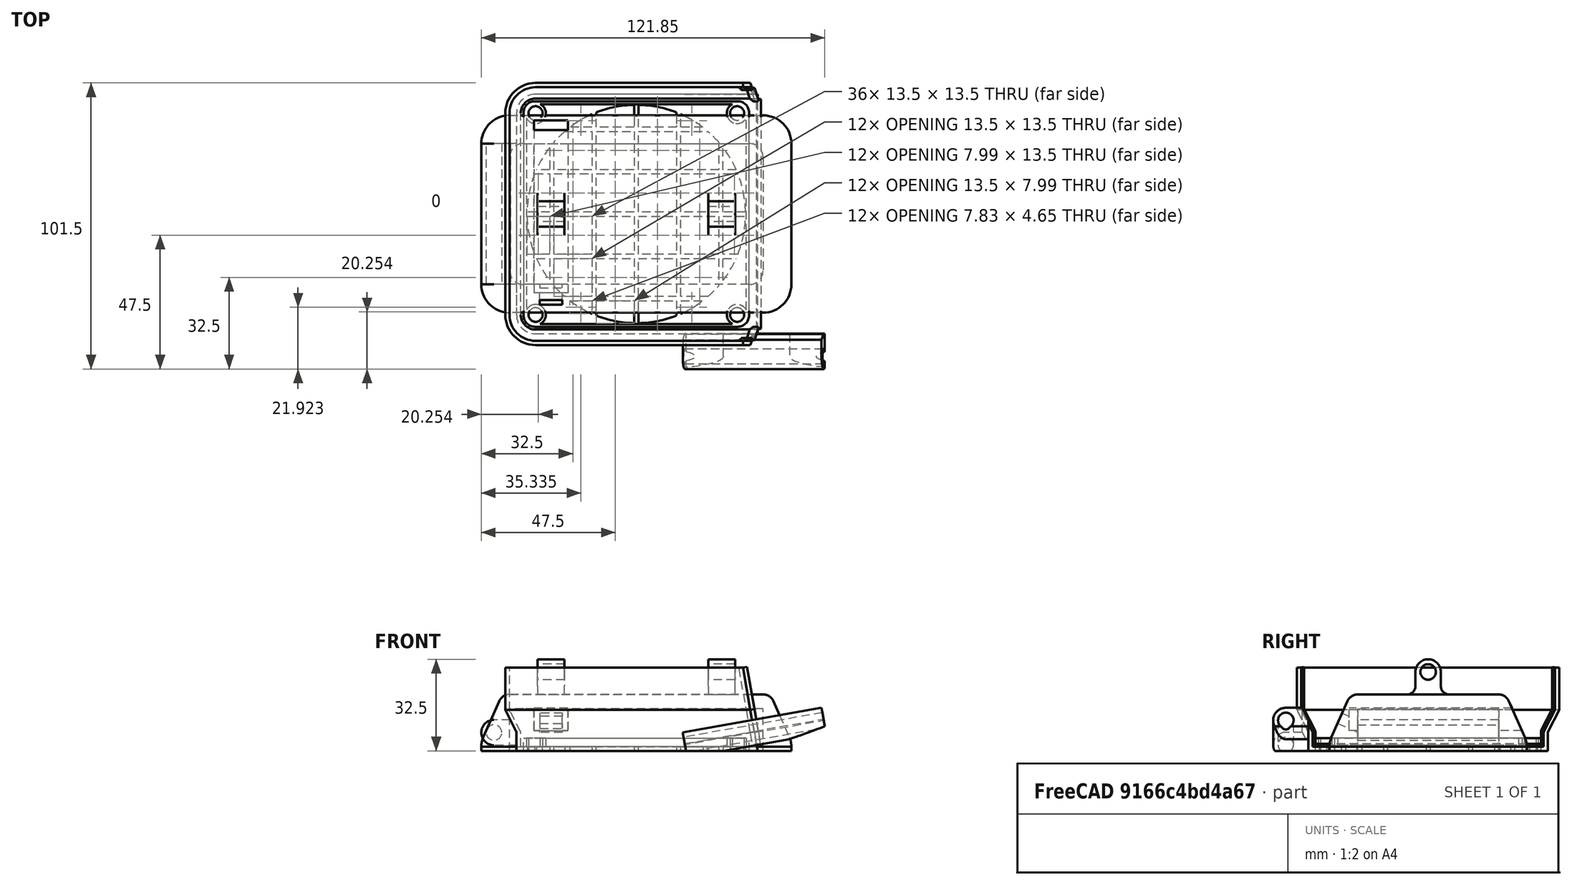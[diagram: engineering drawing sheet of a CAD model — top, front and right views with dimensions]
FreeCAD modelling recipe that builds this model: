
FCSTD DOCUMENT  (FreeCAD 1.0R39285 (Git))
Label: Solder Fume Extractor 2x80mm fans - v2
License: All rights reserved
LicenseURL: https://en.wikipedia.org/wiki/All_rights_reserved
objects: Sketcher::SketchObject×30, PartDesign::Pad×18, PartDesign::CoordinateSystem×13, App::Link×10, PartDesign::Pocket×8, PartDesign::LinearPattern×6, PartDesign::Body×5, PartDesign::AdditivePipe×3, App::DocumentObjectGroup×3, App::FeaturePython×1, Mesh::Feature×1, PartDesign::SubtractivePipe×1, App::Part×1
note: 180 computed .brp shape members not serialized (recipe doc carries the construction recipe); baked Part::Feature solids carry a one-line shape summary decoded from their .brp
EXTERNAL_REF file=Axial Fan.FCStd obj=FanHouse_TopMountHole
EXTERNAL_REF file=Axial Fan.FCStd obj=Assembly

FEATURE [Sketcher::SketchObject] Sketch
  ArcFitTolerance = 1e-06
  AttachmentSupport = -> [XY_Plane]
  FullyConstrained = true
  MakeInternals = false
  MapMode = 5
  sketch-geometry (13):
    g0: LineSegment StartX=-42.5 StartY=35.75 StartZ=0 EndX=-42.5 EndY=-35.75 EndZ=0
    g1: LineSegment StartX=-35.75 StartY=-42.5 StartZ=0 EndX=60 EndY=-42.5 EndZ=0
    g2: LineSegment StartX=60 StartY=-42.5 StartZ=0 EndX=60 EndY=42.5 EndZ=0
    g3: LineSegment StartX=60 StartY=42.5 StartZ=0 EndX=-35.75 EndY=42.5 EndZ=0
    g4: Circle CenterX=-35.75 CenterY=35.75 CenterZ=0 NormalX=0 NormalY=0 NormalZ=1 AngleXU=0 Radius=2.5
    g5: Circle CenterX=35.75 CenterY=35.75 CenterZ=0 NormalX=0 NormalY=0 NormalZ=1 AngleXU=0 Radius=2.5
    g6: Circle CenterX=-35.75 CenterY=-35.75 CenterZ=0 NormalX=0 NormalY=0 NormalZ=1 AngleXU=0 Radius=2.5
    g7: Circle CenterX=35.75 CenterY=-35.75 CenterZ=0 NormalX=0 NormalY=0 NormalZ=1 AngleXU=0 Radius=2.5
    g8: Circle CenterX=0 CenterY=0 CenterZ=0 NormalX=0 NormalY=0 NormalZ=1 AngleXU=0 Radius=38.75
    g9: ArcOfCircle CenterX=-35.75 CenterY=35.75 CenterZ=0 NormalX=0 NormalY=0 NormalZ=1 AngleXU=0 Radius=6.75 StartAngle=1.5708 EndAngle=3.14159
    g10: GeomPoint [constr] X=-42.5 Y=42.5 Z=0
    g11: ArcOfCircle CenterX=-35.75 CenterY=-35.75 CenterZ=0 NormalX=0 NormalY=0 NormalZ=1 AngleXU=0 Radius=6.75 StartAngle=3.14159 EndAngle=4.71239
    g12: GeomPoint [constr] X=-42.5 Y=-42.5 Z=0
  constraints (30):
    c: Coincident(g1,g2)
    c: Coincident(g2,g3)
    c: Vertical(g2)
    c: Horizontal(g1)
    c: Horizontal(g3)
    c: DistanceY(g12,g10) = 85
    c: Equal(g7,g5)
    c: Equal(g5,g4)
    c: Equal(g4,g6)
    c: Diameter(g7) = 5
    c: Symmetric(g7,g5,g-1)
    c: Symmetric(g5,g4,g-2)
    c: Vertical(g6,g4)
    c: Horizontal(g6,g7)
    c: DistanceX(g4,g5) = 71.5
    c: DistanceY(g6,g4) = 71.5
    c: Symmetric(g12,g10,g-1)
    c: Coincident(g8,g-1)
    c: Diameter(g8) = 77.5
    c: DistanceX(g10,g-1) = 42.5
    c: DistanceX(g1) = 60
    c: PointOnObject(g10,g0)
    c: PointOnObject(g10,g3)
    c: Tangent(g0,g9) = -1.5708
    c: Tangent(g3,g9) = -1.5708
    c: PointOnObject(g12,g1)
    c: Tangent(g0,g11) = -1.5708
    c: Tangent(g1,g11) = -1.5708
    c: Equal(g11,g9)
    c: Coincident(g9,g4)
FEATURE [PartDesign::Pad] Pad
  Direction = (0,0,1)
  Length = 1.5
  Length2 = 10
  Profile = -> Sketch
  ReferenceAxis = -> Sketch [N_Axis]
  Refine = true
  Suppressed = false
  Type = 0
FEATURE [Sketcher::SketchObject] Sketch001
  ArcFitTolerance = 1e-06
  AttachmentSupport = -> [Pad]
  ExternalGeometry = -> [Pad]
  FullyConstrained = true
  MakeInternals = false
  MapMode = 5
  Placement = pos=(0,0,1.5) rot=(0,0,1;0rad)
  sketch-geometry (12):
    g0: LineSegment StartX=60 StartY=42.5 StartZ=0 EndX=-35.75 EndY=42.5 EndZ=0
    g1: LineSegment StartX=-42.5 StartY=35.75 StartZ=0 EndX=-42.5 EndY=-35.75 EndZ=0
    g2: LineSegment StartX=-35.75 StartY=-42.5 StartZ=0 EndX=60 EndY=-42.5 EndZ=0
    g3: ArcOfCircle CenterX=-35.75 CenterY=-35.75 CenterZ=0 NormalX=0 NormalY=0 NormalZ=1 AngleXU=0 Radius=6.75 StartAngle=3.14159 EndAngle=4.71239
    g4: ArcOfCircle CenterX=-35.75 CenterY=35.75 CenterZ=0 NormalX=0 NormalY=0 NormalZ=1 AngleXU=0 Radius=6.75 StartAngle=1.5708 EndAngle=3.14159
    g5: LineSegment StartX=60 StartY=-42.5 StartZ=0 EndX=60 EndY=-41 EndZ=0
    g6: LineSegment StartX=60 StartY=-41 StartZ=0 EndX=-35.75 EndY=-41 EndZ=0
    g7: LineSegment StartX=-41 StartY=-35.75 StartZ=0 EndX=-41 EndY=35.75 EndZ=0
    g8: LineSegment StartX=-35.75 StartY=41 StartZ=0 EndX=60 EndY=41 EndZ=0
    g9: LineSegment StartX=60 StartY=41 StartZ=0 EndX=60 EndY=42.5 EndZ=0
    g10: ArcOfCircle CenterX=-35.75 CenterY=-35.75 CenterZ=0 NormalX=0 NormalY=0 NormalZ=1 AngleXU=0 Radius=5.25 StartAngle=3.14159 EndAngle=4.71239
    g11: ArcOfCircle CenterX=-35.75 CenterY=35.75 CenterZ=0 NormalX=0 NormalY=0 NormalZ=1 AngleXU=0 Radius=5.25 StartAngle=1.5708 EndAngle=3.14159
  constraints (30):
    c: Coincident(g0,g-3)
    c: Coincident(g0,g-4)
    c: Horizontal(g2)
    c: Symmetric(g2,g0,g-1)
    c: Equal(g2,g0)
    c: Coincident(g-5,g1)
    c: Coincident(g1,g-5)
    c: Coincident(g3,g2)
    c: Coincident(g3,g1)
    c: Coincident(g4,g1)
    c: Coincident(g4,g0)
    c: Equal(g4,g-4)
    c: Equal(g-4,g3)
    c: Coincident(g5,g2)
    c: Vertical(g5)
    c: Coincident(g6,g5)
    c: Horizontal(g6)
    c: Vertical(g7)
    c: Coincident(g9,g8)
    c: Coincident(g9,g0)
    c: Horizontal(g8)
    c: Vertical(g9)
    c: Equal(g5,g9)
    c: Equal(g6,g8)
    c: Tangent(g10,g6) = 1.5708
    c: Tangent(g10,g7) = 1.5708
    c: Tangent(g11,g7) = 1.5708
    c: Tangent(g11,g8) = 1.5708
    c: DistanceY(g5,g5) = 1.5
    c: Coincident(g11,g4)
FEATURE [PartDesign::Pad] Pad001
  BaseFeature = -> Pad
  Direction = (0,0,1)
  Length = 5
  Length2 = 10
  Profile = -> Sketch001
  ReferenceAxis = -> Sketch001 [N_Axis]
  Refine = true
  Suppressed = false
  Type = 0
FEATURE [Sketcher::SketchObject] Sketch002
  ArcFitTolerance = 1e-06
  AttachmentSupport = -> [Pad001]
  ExternalGeometry = -> [Pad001]
  FullyConstrained = true
  MakeInternals = false
  MapMode = 5
  Placement = pos=(60,0,0) rot=(0.57735,0.57735,0.57735;2.0944rad)
  sketch-geometry (9):
    g0: LineSegment StartX=41.1112 StartY=6.9583 StartZ=0 EndX=45 EndY=14.5 EndZ=0
    g1: LineSegment [constr] StartX=45 StartY=14.5 StartZ=0 EndX=46.5 EndY=14.5 EndZ=0
    g2: LineSegment StartX=46.5 StartY=14.5 StartZ=0 EndX=42.6112 EndY=6.9583 EndZ=0
    g3: ArcOfCircle CenterX=43.5 CenterY=6.5 CenterZ=0 NormalX=0 NormalY=0 NormalZ=1 AngleXU=0 Radius=1 StartAngle=2.66551 EndAngle=3.14159
    g4: ArcOfCircle CenterX=42 CenterY=6.5 CenterZ=0 NormalX=0 NormalY=0 NormalZ=1 AngleXU=0 Radius=1 StartAngle=2.66551 EndAngle=3.14159
    g5: LineSegment StartX=42.5 StartY=6.5 StartZ=0 EndX=41 EndY=6.5 EndZ=0
    g6: LineSegment StartX=45 StartY=14.5 StartZ=0 EndX=45 EndY=29.5 EndZ=0
    g7: LineSegment StartX=45 StartY=29.5 StartZ=0 EndX=46.5 EndY=29.5 EndZ=0
    g8: LineSegment StartX=46.5 StartY=29.5 StartZ=0 EndX=46.5 EndY=14.5 EndZ=0
  constraints (24):
    c: Coincident(g0,g1)
    c: Horizontal(g1)
    c: Coincident(g1,g2)
    c: Coincident(g3,g-3)
    c: Coincident(g4,g-3)
    c: Tangent(g4,g0) = 1.5708
    c: Tangent(g3,g2) = -1.5708
    c: Coincident(g5,g3)
    c: Coincident(g5,g4)
    c: Perpendicular(g3,g5)
    c: Perpendicular(g4,g5)
    c: Equal(g1,g5)
    c: Radius(g4) = 1
    c: DistanceY(g3,g1) = 8
    c: DistanceX(g3,g1) = 4
    c: Equal(g4,g3)
    c: Coincident(g0,g6)
    c: Vertical(g6)
    c: Coincident(g6,g7)
    c: Coincident(g7,g8)
    c: Coincident(g8,g1)
    c: Vertical(g8)
    c: Horizontal(g7)
    c: DistanceY(g8,g8) = 15
FEATURE [PartDesign::AdditivePipe] AdditivePipe
  AuxilleryCurvelinear = true
  AuxillerySpineTangent = false
  BaseFeature = -> Pad001
  Binormal = (0,0,0)
  Mode = 0
  Profile = -> Sketch002
  Refine = true
  Spine = -> Pad001 [Edge32,Edge33,Edge34,Edge35,Edge36]
  SpineTangent = false
  Suppressed = false
  Transformation = 0
  Transition = 0
FEATURE [Sketcher::SketchObject] Sketch003
  ArcFitTolerance = 1e-06
  AttachmentSupport = -> [XY_Plane]
  ExternalGeometry = -> [AdditivePipe]
  FullyConstrained = true
  MakeInternals = false
  MapMode = 5
  sketch-geometry (5):
    g0: LineSegment StartX=-30.75 StartY=42.5 StartZ=0 EndX=-30.75 EndY=-42.5 EndZ=0
    g1: LineSegment StartX=-30.75 StartY=-42.5 StartZ=0 EndX=-29.25 EndY=-42.5 EndZ=0
    g2: LineSegment StartX=-29.25 StartY=-42.5 StartZ=0 EndX=-29.25 EndY=42.5 EndZ=0
    g3: LineSegment StartX=-29.25 StartY=42.5 StartZ=0 EndX=-30.75 EndY=42.5 EndZ=0
    g4: GeomPoint [constr] X=-30 Y=0 Z=0
  constraints (13):
    c: Coincident(g0,g1)
    c: Coincident(g1,g2)
    c: Coincident(g2,g3)
    c: Coincident(g3,g0)
    c: Vertical(g0)
    c: Vertical(g2)
    c: Horizontal(g1)
    c: Horizontal(g3)
    c: Symmetric(g2,g0,g4)
    c: PointOnObject(g4,g-1)
    c: PointOnObject(g1,g-3)
    c: DistanceX(g3,g3) = 1.5
    c: DistanceX(g4,g-1) = 30
FEATURE [PartDesign::Pad] Pad002
  BaseFeature = -> AdditivePipe
  Direction = (0,0,1)
  Length = 10
  Length2 = 10
  Profile = -> Sketch003
  ReferenceAxis = -> Sketch003 [N_Axis]
  Refine = true
  Suppressed = false
  Type = 3
  UpToFace = -> AdditivePipe [Face4]
FEATURE [PartDesign::LinearPattern] LinearPattern
  BaseFeature = -> Pad002
  Direction = -> Sketch003 [H_Axis]
  Length = 60
  Mode = 0
  Occurrences = 5
  Offset = 15
  Originals = -> [Pad002]
  Refine = true
  Suppressed = false
  TransformMode = 0
FEATURE [Sketcher::SketchObject] Sketch004
  ArcFitTolerance = 1e-06
  AttachmentSupport = -> [XY_Plane]
  ExternalGeometry = -> [LinearPattern]
  FullyConstrained = true
  MakeInternals = false
  MapMode = 5
  sketch-geometry (5):
    g0: LineSegment StartX=42.5 StartY=29.25 StartZ=0 EndX=42.5 EndY=30.75 EndZ=0
    g1: LineSegment StartX=42.5 StartY=30.75 StartZ=0 EndX=-42.5 EndY=30.75 EndZ=0
    g2: LineSegment StartX=-42.5 StartY=30.75 StartZ=0 EndX=-42.5 EndY=29.25 EndZ=0
    g3: LineSegment StartX=-42.5 StartY=29.25 StartZ=0 EndX=42.5 EndY=29.25 EndZ=0
    g4: GeomPoint [constr] X=0 Y=30 Z=0
  constraints (13):
    c: Coincident(g0,g1)
    c: Coincident(g1,g2)
    c: Coincident(g2,g3)
    c: Coincident(g3,g0)
    c: Vertical(g0)
    c: Vertical(g2)
    c: Horizontal(g1)
    c: Horizontal(g3)
    c: Symmetric(g2,g0,g4)
    c: PointOnObject(g4,g-2)
    c: PointOnObject(g1,g-3)
    c: DistanceY(g4) = 30
    c: DistanceY(g0,g0) = 1.5
FEATURE [PartDesign::Pad] Pad003
  BaseFeature = -> LinearPattern
  Direction = (0,0,1)
  Length = 10
  Length2 = 10
  Profile = -> Sketch004
  ReferenceAxis = -> Sketch004 [N_Axis]
  Refine = true
  Suppressed = false
  Type = 3
  UpToFace = -> LinearPattern [Face68]
FEATURE [PartDesign::LinearPattern] LinearPattern001
  BaseFeature = -> Pad003
  Direction = -> Sketch004 [V_Axis]
  Length = 60
  Mode = 0
  Occurrences = 5
  Offset = 15
  Originals = -> [Pad003]
  Refine = true
  Reversed = true
  Suppressed = false
  TransformMode = 0
FEATURE [PartDesign::CoordinateSystem] FanMountHole
  AttacherType = Attacher::AttachEngine3D
  AttachmentSupport = -> [LinearPattern001]
  MapMode = 11
  Placement = pos=(-35.75,-35.75,0) rot=(0,0,1;1.5708rad)
FEATURE [PartDesign::CoordinateSystem] LCS_Origin
  AttacherType = Attacher::AttachEngine3D
  AttachmentSupport = -> [X_Axis001]
  MapMode = 2
FEATURE [App::DocumentObjectGroup] Constraints
FEATURE [App::FeaturePython] Variables  # WARN: FeaturePython — macro-defined, semantics opaque (R4)
  Type = App::PropertyContainer
FEATURE [App::DocumentObjectGroup] Configurations
FEATURE [Sketcher::SketchObject] Sketch005
  ArcFitTolerance = 1e-06
  AttachmentSupport = -> [XZ_Plane]
  ExternalGeometry = -> [LinearPattern001]
  FullyConstrained = true
  MakeInternals = false
  MapMode = 5
  Placement = pos=(0,0,0) rot=(1,0,0;1.5708rad)
  sketch-geometry (4):
    g0: LineSegment StartX=60 StartY=29.5 StartZ=0 EndX=60 EndY=0 EndZ=0
    g1: LineSegment StartX=60 StartY=0 StartZ=0 EndX=43 EndY=0 EndZ=0
    g2: LineSegment StartX=43 StartY=0 StartZ=0 EndX=37.7984 EndY=29.5 EndZ=0
    g3: LineSegment StartX=37.7984 StartY=29.5 StartZ=0 EndX=60 EndY=29.5 EndZ=0
  constraints (11):
    c: PointOnObject(g0,g-1)
    c: Vertical(g0)
    c: Coincident(g0,g1)
    c: PointOnObject(g1,g-1)
    c: Coincident(g1,g2)
    c: Coincident(g2,g3)
    c: Coincident(g3,g0)
    c: DistanceX(g-1,g1) = 43
    c: Angle(g1,g2) = 1.74533
    c: Coincident(g0,g-3)
    c: PointOnObject(g2,g-3)
FEATURE [PartDesign::Pocket] Pocket
  BaseFeature = -> LinearPattern001
  Direction = (0,1,-2e-16)
  Length = 5
  Length2 = 5
  Midplane = true
  Profile = -> Sketch005
  ReferenceAxis = -> Sketch005 [N_Axis]
  Refine = true
  Suppressed = false
  Type = 1
FEATURE [PartDesign::CoordinateSystem] OtherFanHolder
  AttacherType = Attacher::AttachEngine3D
  AttachmentSupport = -> [Pocket]
  MapMode = 45
  Placement = pos=(42.8701,0,0.736527) rot=(0.642788,0,0.766044;3.14159rad)
FEATURE [PartDesign::CoordinateSystem] FilterHolderMount
  AttacherType = Attacher::AttachEngine3D
  AttachmentSupport = -> [Pocket]
  MapMode = 11
  Placement = pos=(-35.75,35.75,1.5) rot=(0,0,1;1.5708rad)
FEATURE [Sketcher::SketchObject] Sketch006
  ArcFitTolerance = 1e-06
  AttachmentSupport = -> [XY_Plane002]
  FullyConstrained = true
  MakeInternals = false
  MapMode = 5
  sketch-geometry (15):
    g0: LineSegment StartX=40 StartY=-36 StartZ=0 EndX=40 EndY=36 EndZ=0
    g1: LineSegment StartX=36 StartY=40 StartZ=0 EndX=-36 EndY=40 EndZ=0
    g2: LineSegment StartX=-40 StartY=36 StartZ=0 EndX=-40 EndY=-36 EndZ=0
    g3: LineSegment StartX=-36 StartY=-40 StartZ=0 EndX=36 EndY=-40 EndZ=0
    g4: ArcOfCircle CenterX=36 CenterY=-36 CenterZ=0 NormalX=0 NormalY=0 NormalZ=1 AngleXU=0 Radius=4 StartAngle=4.71239 EndAngle=6.28319
    g5: ArcOfCircle CenterX=36 CenterY=36 CenterZ=0 NormalX=0 NormalY=0 NormalZ=1 AngleXU=0 Radius=4 StartAngle=2e-16 EndAngle=1.5708
    g6: ArcOfCircle CenterX=-36 CenterY=36 CenterZ=0 NormalX=0 NormalY=0 NormalZ=1 AngleXU=0 Radius=4 StartAngle=1.5708 EndAngle=3.14159
    g7: ArcOfCircle CenterX=-36 CenterY=-36 CenterZ=0 NormalX=0 NormalY=0 NormalZ=1 AngleXU=0 Radius=4 StartAngle=3.14159 EndAngle=4.71239
    g8: GeomPoint [constr] X=40 Y=-40 Z=0
    g9: GeomPoint [constr] X=-40 Y=40 Z=0
    g10: Circle CenterX=-35.75 CenterY=35.75 CenterZ=0 NormalX=0 NormalY=0 NormalZ=1 AngleXU=0 Radius=2.5
    g11: Circle CenterX=35.75 CenterY=35.75 CenterZ=0 NormalX=0 NormalY=0 NormalZ=1 AngleXU=0 Radius=2.5
    g12: Circle CenterX=35.75 CenterY=-35.75 CenterZ=0 NormalX=0 NormalY=0 NormalZ=1 AngleXU=0 Radius=2.5
    g13: Circle CenterX=-35.75 CenterY=-35.75 CenterZ=0 NormalX=0 NormalY=0 NormalZ=1 AngleXU=0 Radius=2.5
    g14: Circle CenterX=0 CenterY=0 CenterZ=0 NormalX=0 NormalY=0 NormalZ=1 AngleXU=0 Radius=38.75
  constraints (34):
    c: Tangent(g0,g4) = -1.5708
    c: Tangent(g0,g5) = -1.5708
    c: Tangent(g1,g5) = -1.5708
    c: Tangent(g1,g6) = -1.5708
    c: Tangent(g2,g6) = -1.5708
    c: Tangent(g2,g7) = -1.5708
    c: Tangent(g3,g7) = -1.5708
    c: Tangent(g3,g4) = -1.5708
    c: Vertical(g2)
    c: Horizontal(g1)
    c: Equal(g4,g5)
    c: Equal(g5,g6)
    c: Equal(g6,g7)
    c: PointOnObject(g8,g0)
    c: PointOnObject(g8,g3)
    c: PointOnObject(g9,g1)
    c: PointOnObject(g9,g2)
    c: Radius(g7) = 4
    c: Symmetric(g3,g3,g-2)
    c: Symmetric(g0,g0,g-1)
    c: Equal(g0,g3)
    c: DistanceY(g3,g1) = 80
    c: Equal(g10,g11)
    c: Equal(g11,g12)
    c: Equal(g12,g13)
    c: Symmetric(g10,g11,g-2)
    c: Symmetric(g11,g12,g-1)
    c: Horizontal(g12,g13)
    c: Vertical(g13,g10)
    c: DistanceY(g13,g10) = 71.5
    c: DistanceX(g10,g11) = 71.5
    c: Diameter(g11) = 5
    c: Coincident(g14,g-1)
    c: Diameter(g14) = 77.5
FEATURE [PartDesign::Pad] Pad004
  Direction = (0,0,1)
  Length = 1.5
  Length2 = 10
  Profile = -> Sketch006
  ReferenceAxis = -> Sketch006 [N_Axis]
  Refine = true
  Suppressed = false
  Type = 0
FEATURE [Sketcher::SketchObject] Sketch007
  ArcFitTolerance = 1e-06
  AttachmentSupport = -> [XY_Plane002]
  ExternalGeometry = -> [Pad004]
  FullyConstrained = true
  MakeInternals = false
  MapMode = 5
  sketch-geometry (5):
    g0: LineSegment StartX=-29.25 StartY=-40 StartZ=0 EndX=-29.25 EndY=40 EndZ=0
    g1: LineSegment StartX=-29.25 StartY=40 StartZ=0 EndX=-30.75 EndY=40 EndZ=0
    g2: LineSegment StartX=-30.75 StartY=40 StartZ=0 EndX=-30.75 EndY=-40 EndZ=0
    g3: LineSegment StartX=-30.75 StartY=-40 StartZ=0 EndX=-29.25 EndY=-40 EndZ=0
    g4: GeomPoint [constr] X=-30 Y=0 Z=0
  constraints (13):
    c: Coincident(g0,g1)
    c: Coincident(g1,g2)
    c: Coincident(g2,g3)
    c: Coincident(g3,g0)
    c: Vertical(g0)
    c: Vertical(g2)
    c: Horizontal(g1)
    c: Horizontal(g3)
    c: Symmetric(g2,g0,g4)
    c: PointOnObject(g4,g-1)
    c: PointOnObject(g1,g-3)
    c: DistanceX(g4,g-1) = 30
    c: DistanceX(g1,g1) = 1.5
FEATURE [PartDesign::Pad] Pad005
  BaseFeature = -> Pad004
  Direction = (0,0,1)
  Length = 10
  Length2 = 10
  Profile = -> Sketch007
  ReferenceAxis = -> Sketch007 [N_Axis]
  Refine = true
  Suppressed = false
  Type = 3
  UpToFace = -> Pad004 [Face15]
FEATURE [PartDesign::LinearPattern] LinearPattern002
  BaseFeature = -> Pad005
  Direction = -> Sketch007 [H_Axis]
  Length = 60
  Mode = 0
  Occurrences = 5
  Offset = 15
  Originals = -> [Pad005]
  Refine = true
  Suppressed = false
  TransformMode = 0
FEATURE [Sketcher::SketchObject] Sketch008
  ArcFitTolerance = 1e-06
  AttachmentSupport = -> [XY_Plane002]
  ExternalGeometry = -> [LinearPattern002]
  FullyConstrained = true
  MakeInternals = false
  MapMode = 5
  sketch-geometry (5):
    g0: LineSegment StartX=40 StartY=-30.75 StartZ=0 EndX=40 EndY=-29.25 EndZ=0
    g1: LineSegment StartX=40 StartY=-29.25 StartZ=0 EndX=-40 EndY=-29.25 EndZ=0
    g2: LineSegment StartX=-40 StartY=-29.25 StartZ=0 EndX=-40 EndY=-30.75 EndZ=0
    g3: LineSegment StartX=-40 StartY=-30.75 StartZ=0 EndX=40 EndY=-30.75 EndZ=0
    g4: GeomPoint [constr] X=0 Y=-30 Z=0
  constraints (13):
    c: Coincident(g0,g1)
    c: Coincident(g1,g2)
    c: Coincident(g2,g3)
    c: Coincident(g3,g0)
    c: Vertical(g0)
    c: Vertical(g2)
    c: Horizontal(g1)
    c: Horizontal(g3)
    c: Symmetric(g2,g0,g4)
    c: PointOnObject(g4,g-2)
    c: PointOnObject(g1,g-3)
    c: DistanceY(g4,g-1) = 30
    c: DistanceY(g0,g0) = 1.5
FEATURE [PartDesign::Pad] Pad006
  BaseFeature = -> LinearPattern002
  Direction = (0,0,1)
  Length = 10
  Length2 = 10
  Profile = -> Sketch008
  ReferenceAxis = -> Sketch008 [N_Axis]
  Refine = true
  Suppressed = false
  Type = 3
  UpToFace = -> LinearPattern002 [Face32]
FEATURE [PartDesign::LinearPattern] LinearPattern003
  BaseFeature = -> Pad006
  Direction = -> Sketch008 [V_Axis]
  Length = 60
  Mode = 0
  Occurrences = 5
  Offset = 15
  Originals = -> [Pad006]
  Refine = true
  Suppressed = false
  TransformMode = 0
FEATURE [Sketcher::SketchObject] Sketch009
  ArcFitTolerance = 1e-06
  AttachmentSupport = -> [LinearPattern003]
  ExternalGeometry = -> [LinearPattern003]
  FullyConstrained = true
  MakeInternals = false
  MapMode = 5
  Placement = pos=(0,0,1.5) rot=(0,0,1;0rad)
  sketch-geometry (20):
    g0: LineSegment StartX=-40 StartY=36 StartZ=0 EndX=-40 EndY=-36 EndZ=0
    g1: LineSegment StartX=-36 StartY=-40 StartZ=0 EndX=36 EndY=-40 EndZ=0
    g2: LineSegment StartX=40 StartY=-36 StartZ=0 EndX=40 EndY=36 EndZ=0
    g3: LineSegment StartX=36 StartY=40 StartZ=0 EndX=-36 EndY=40 EndZ=0
    g4: ArcOfCircle CenterX=-36 CenterY=36 CenterZ=0 NormalX=0 NormalY=0 NormalZ=1 AngleXU=0 Radius=4 StartAngle=1.5708 EndAngle=3.14159
    g5: ArcOfCircle CenterX=-36 CenterY=-36 CenterZ=0 NormalX=0 NormalY=0 NormalZ=1 AngleXU=0 Radius=4 StartAngle=3.14159 EndAngle=4.71239
    g6: ArcOfCircle CenterX=36 CenterY=-36 CenterZ=0 NormalX=0 NormalY=0 NormalZ=1 AngleXU=0 Radius=4 StartAngle=4.71239 EndAngle=6.28319
    g7: ArcOfCircle CenterX=36 CenterY=36 CenterZ=0 NormalX=0 NormalY=0 NormalZ=1 AngleXU=0 Radius=4 StartAngle=-9e-16 EndAngle=1.5708
    g8: GeomPoint [constr] X=-40 Y=40 Z=0
    g9: GeomPoint [constr] X=40 Y=-40 Z=0
    g10: LineSegment StartX=-39 StartY=36 StartZ=0 EndX=-39 EndY=-36 EndZ=0
    g11: LineSegment StartX=-36 StartY=-39 StartZ=0 EndX=36 EndY=-39 EndZ=0
    g12: LineSegment StartX=39 StartY=-36 StartZ=0 EndX=39 EndY=36 EndZ=0
    g13: LineSegment StartX=36 StartY=39 StartZ=0 EndX=-36 EndY=39 EndZ=0
    g14: ArcOfCircle CenterX=-36 CenterY=36 CenterZ=0 NormalX=0 NormalY=0 NormalZ=1 AngleXU=0 Radius=3 StartAngle=1.5708 EndAngle=3.14159
    g15: ArcOfCircle CenterX=-36 CenterY=-36 CenterZ=0 NormalX=0 NormalY=0 NormalZ=1 AngleXU=0 Radius=3 StartAngle=3.14159 EndAngle=4.71239
    g16: ArcOfCircle CenterX=36 CenterY=-36 CenterZ=0 NormalX=0 NormalY=0 NormalZ=1 AngleXU=0 Radius=3 StartAngle=4.71239 EndAngle=6.28319
    g17: ArcOfCircle CenterX=36 CenterY=36 CenterZ=0 NormalX=0 NormalY=0 NormalZ=1 AngleXU=0 Radius=3 StartAngle=-9e-16 EndAngle=1.5708
    g18: GeomPoint [constr] X=-39 Y=39 Z=0
    g19: GeomPoint [constr] X=39 Y=-39 Z=0
  constraints (44):
    c: Tangent(g0,g4) = -1.5708
    c: Tangent(g0,g5) = -1.5708
    c: Tangent(g1,g5) = -1.5708
    c: Tangent(g1,g6) = -1.5708
    c: Tangent(g2,g6) = -1.5708
    c: Tangent(g2,g7) = -1.5708
    c: Tangent(g3,g7) = -1.5708
    c: Tangent(g3,g4) = -1.5708
    c: Vertical(g0)
    c: Vertical(g2)
    c: Horizontal(g1)
    c: Equal(g4,g5)
    c: Equal(g5,g6)
    c: Equal(g6,g7)
    c: PointOnObject(g8,g0)
    c: PointOnObject(g8,g3)
    c: PointOnObject(g9,g1)
    c: PointOnObject(g9,g2)
    c: Coincident(g3,g-5)
    c: Equal(g-5,g7)
    c: Coincident(g3,g-3)
    c: Equal(g3,g2)
    c: Tangent(g10,g14) = -1.5708
    c: Tangent(g10,g15) = -1.5708
    c: Tangent(g11,g15) = -1.5708
    c: Tangent(g11,g16) = -1.5708
    c: Tangent(g12,g16) = -1.5708
    c: Tangent(g12,g17) = -1.5708
    c: Tangent(g13,g17) = -1.5708
    c: Tangent(g13,g14) = -1.5708
    c: Vertical(g10)
    c: Horizontal(g11)
    c: Equal(g14,g15)
    c: Equal(g15,g16)
    c: Equal(g16,g17)
    c: PointOnObject(g18,g10)
    c: PointOnObject(g18,g13)
    c: PointOnObject(g19,g11)
    c: PointOnObject(g19,g12)
    c: Symmetric(g12,g12,g-1)
    c: Symmetric(g13,g13,g-2)
    c: Equal(g11,g12)
    c: DistanceX(g12,g2) = 1
    c: Horizontal(g2,g12)
FEATURE [PartDesign::Pad] Pad007
  BaseFeature = -> LinearPattern003
  Direction = (0,0,1)
  Length = 3
  Length2 = 10
  Profile = -> Sketch009
  ReferenceAxis = -> Sketch009 [N_Axis]
  Refine = true
  Suppressed = false
  Type = 0
FEATURE [PartDesign::CoordinateSystem] FanHolder
  AttacherType = Attacher::AttachEngine3D
  AttachmentOffset = pos=(0,0,3) rot=(0,0,1;0rad)
  AttachmentSupport = -> [Pad007]
  MapMode = 11
  Placement = pos=(-35.75,35.75,4.5) rot=(0,0,1;1.5708rad)
FEATURE [Sketcher::SketchObject] Sketch010
  ArcFitTolerance = 1e-06
  AttachmentSupport = -> [XZ_Plane]
  ExternalGeometry = -> [Pocket]
  FullyConstrained = true
  MakeInternals = false
  MapMode = 5
  Placement = pos=(0,0,0) rot=(1,0,0;1.5708rad)
  sketch-geometry (7):
    g0: ArcOfCircle CenterX=-43.5 CenterY=6.5 CenterZ=0 NormalX=0 NormalY=0 NormalZ=1 AngleXU=0 Radius=1 StartAngle=-2.4e-14 EndAngle=0.476081
    g1: LineSegment StartX=-42.5 StartY=6.5 StartZ=0 EndX=-42.5 EndY=2 EndZ=0
    g2: LineSegment StartX=-42.5 StartY=2 StartZ=0 EndX=-50.5 EndY=2 EndZ=0
    g3: LineSegment StartX=-42.6112 StartY=6.9583 StartZ=0 EndX=-44.6953 EndY=11 EndZ=0
    g4: LineSegment StartX=-44.6953 StartY=11 StartZ=0 EndX=-50.5 EndY=11 EndZ=0
    g5: ArcOfCircle CenterX=-50.5 CenterY=6.5 CenterZ=0 NormalX=0 NormalY=0 NormalZ=1 AngleXU=0 Radius=4.5 StartAngle=1.5708 EndAngle=4.71239
    g6: Circle CenterX=-50.5 CenterY=6.5 CenterZ=0 NormalX=0 NormalY=0 NormalZ=1 AngleXU=0 Radius=2.75
  constraints (18):
    c: Coincident(g0,g-5)
    c: Coincident(g0,g-5)
    c: Equal(g-5,g0)
    c: Coincident(g1,g0)
    c: PointOnObject(g1,g-3)
    c: Coincident(g2,g1)
    c: Horizontal(g2)
    c: Coincident(g3,g0)
    c: PointOnObject(g3,g-4)
    c: Horizontal(g4)
    c: Tangent(g5,g4) = -1.5708
    c: Tangent(g5,g2) = 1.5708
    c: Diameter(g5) = 9
    c: Diameter(g6) = 5.5
    c: Coincident(g6,g5)
    c: Horizontal(g0,g5)
    c: Coincident(g3,g4)
    c: DistanceX(g5,g-4) = 4
FEATURE [PartDesign::Pad] Pad008
  BaseFeature = -> Pocket
  Direction = (0,-1,2e-16)
  Length = 50
  Length2 = 10
  Midplane = true
  Profile = -> Sketch010
  ReferenceAxis = -> Sketch010 [N_Axis]
  Refine = true
  Suppressed = false
  Type = 0
FEATURE [Sketcher::SketchObject] Sketch011
  ArcFitTolerance = 1e-06
  AttachmentSupport = -> [Pad008]
  ExternalGeometry = -> [Pad008]
  FullyConstrained = true
  MakeInternals = false
  MapMode = 5
  Placement = pos=(41.7034,1.6e-15,7.35343) rot=(0.540716,0.540716,0.6444;1.99673rad)
  sketch-geometry (7):
    g0: ArcOfCircle CenterX=-43.0908 CenterY=-0.761797 CenterZ=0 NormalX=0 NormalY=0 NormalZ=1 AngleXU=0 Radius=0.6 StartAngle=6.10761 EndAngle=6.92787
    g1: LineSegment StartX=-44.66 StartY=3.6334 StartZ=0 EndX=-42.6112 EndY=-0.401229 EndZ=0
    g2: LineSegment StartX=-42.5 StartY=-5.3666 StartZ=0 EndX=-42.5 EndY=-0.866599 EndZ=0
    g3: LineSegment StartX=-42.5 StartY=-5.3666 StartZ=0 EndX=-50.5 EndY=-5.3666 EndZ=0
    g4: LineSegment StartX=-44.66 StartY=3.6334 StartZ=0 EndX=-50.5 EndY=3.6334 EndZ=0
    g5: ArcOfCircle CenterX=-50.5 CenterY=-0.866599 CenterZ=0 NormalX=0 NormalY=0 NormalZ=1 AngleXU=0 Radius=4.5 StartAngle=1.5708 EndAngle=4.71239
    g6: Circle CenterX=-50.5 CenterY=-0.866599 CenterZ=0 NormalX=0 NormalY=0 NormalZ=1 AngleXU=0 Radius=2.75
  constraints (18):
    c: Coincident(g0,g-3)
    c: Coincident(g0,g-4)
    c: Radius(g0) = 0.6
    c: Coincident(g3,g2)
    c: Horizontal(g3)
    c: Coincident(g4,g1)
    c: Horizontal(g4)
    c: Tangent(g5,g4) = -1.5708
    c: Tangent(g5,g3) = 1.5708
    c: Diameter(g5) = 9
    c: Horizontal(g5,g2)
    c: Coincident(g6,g5)
    c: Diameter(g6) = 5.5
    c: DistanceX(g5,g-4) = 4
    c: Coincident(g2,g0)
    c: PointOnObject(g1,g-4)
    c: PointOnObject(g2,g-3)
    c: Coincident(g0,g1)
FEATURE [PartDesign::Pad] Pad009
  BaseFeature = -> Pad008
  Direction = (0.984808,-1e-16,0.173648)
  Length = 50
  Length2 = 10
  Midplane = true
  Profile = -> Sketch011
  ReferenceAxis = -> Sketch011 [N_Axis]
  Refine = true
  Suppressed = false
  Type = 0
FEATURE [Mesh::Feature] base_mount
FEATURE [Sketcher::SketchObject] Sketch014
  ArcFitTolerance = 1e-06
  AttachmentSupport = -> [XY_Plane004]
  FullyConstrained = true
  MakeInternals = false
  MapMode = 5
  sketch-geometry (13):
    g0: LineSegment StartX=-42.5 StartY=35.75 StartZ=0 EndX=-42.5 EndY=-35.75 EndZ=0
    g1: LineSegment StartX=-35.75 StartY=-42.5 StartZ=0 EndX=60 EndY=-42.5 EndZ=0
    g2: LineSegment StartX=60 StartY=-42.5 StartZ=0 EndX=60 EndY=42.5 EndZ=0
    g3: LineSegment StartX=60 StartY=42.5 StartZ=0 EndX=-35.75 EndY=42.5 EndZ=0
    g4: Circle CenterX=-35.75 CenterY=35.75 CenterZ=0 NormalX=0 NormalY=0 NormalZ=1 AngleXU=0 Radius=2.5
    g5: Circle CenterX=35.75 CenterY=35.75 CenterZ=0 NormalX=0 NormalY=0 NormalZ=1 AngleXU=0 Radius=2.5
    g6: Circle CenterX=-35.75 CenterY=-35.75 CenterZ=0 NormalX=0 NormalY=0 NormalZ=1 AngleXU=0 Radius=2.5
    g7: Circle CenterX=35.75 CenterY=-35.75 CenterZ=0 NormalX=0 NormalY=0 NormalZ=1 AngleXU=0 Radius=2.5
    g8: Circle CenterX=0 CenterY=0 CenterZ=0 NormalX=0 NormalY=0 NormalZ=1 AngleXU=0 Radius=38.75
    g9: ArcOfCircle CenterX=-35.75 CenterY=35.75 CenterZ=0 NormalX=0 NormalY=0 NormalZ=1 AngleXU=0 Radius=6.75 StartAngle=1.5708 EndAngle=3.14159
    g10: GeomPoint [constr] X=-42.5 Y=42.5 Z=0
    g11: ArcOfCircle CenterX=-35.75 CenterY=-35.75 CenterZ=0 NormalX=0 NormalY=0 NormalZ=1 AngleXU=0 Radius=6.75 StartAngle=3.14159 EndAngle=4.71239
    g12: GeomPoint [constr] X=-42.5 Y=-42.5 Z=0
  constraints (30):
    c: Coincident(g1,g2)
    c: Coincident(g2,g3)
    c: Vertical(g2)
    c: Horizontal(g1)
    c: Horizontal(g3)
    c: DistanceY(g12,g10) = 85
    c: Equal(g7,g5)
    c: Equal(g5,g4)
    c: Equal(g4,g6)
    c: Diameter(g7) = 5
    c: Symmetric(g7,g5,g-1)
    c: Symmetric(g5,g4,g-2)
    c: Vertical(g6,g4)
    c: Horizontal(g6,g7)
    c: DistanceX(g4,g5) = 71.5
    c: DistanceY(g6,g4) = 71.5
    c: Symmetric(g12,g10,g-1)
    c: Coincident(g8,g-1)
    c: Diameter(g8) = 77.5
    c: DistanceX(g10,g-1) = 42.5
    c: DistanceX(g1) = 60
    c: PointOnObject(g10,g0)
    c: PointOnObject(g10,g3)
    c: Tangent(g0,g9) = -1.5708
    c: Tangent(g3,g9) = -1.5708
    c: PointOnObject(g12,g1)
    c: Tangent(g0,g11) = -1.5708
    c: Tangent(g1,g11) = -1.5708
    c: Equal(g11,g9)
    c: Coincident(g9,g4)
FEATURE [PartDesign::Pad] Pad010
  Direction = (0,0,1)
  Length = 1.5
  Length2 = 10
  Profile = -> Sketch014
  ReferenceAxis = -> Sketch014 [N_Axis]
  Refine = true
  Suppressed = false
  Type = 0
FEATURE [Sketcher::SketchObject] Sketch015
  ArcFitTolerance = 1e-06
  AttachmentSupport = -> [Pad010]
  ExternalGeometry = -> [Pad010]
  FullyConstrained = true
  MakeInternals = false
  MapMode = 5
  Placement = pos=(0,0,1.5) rot=(0,0,1;0rad)
  sketch-geometry (12):
    g0: LineSegment StartX=60 StartY=42.5 StartZ=0 EndX=-35.75 EndY=42.5 EndZ=0
    g1: LineSegment StartX=-42.5 StartY=35.75 StartZ=0 EndX=-42.5 EndY=-35.75 EndZ=0
    g2: LineSegment StartX=-35.75 StartY=-42.5 StartZ=0 EndX=60 EndY=-42.5 EndZ=0
    g3: ArcOfCircle CenterX=-35.75 CenterY=-35.75 CenterZ=0 NormalX=0 NormalY=0 NormalZ=1 AngleXU=0 Radius=6.75 StartAngle=3.14159 EndAngle=4.71239
    g4: ArcOfCircle CenterX=-35.75 CenterY=35.75 CenterZ=0 NormalX=0 NormalY=0 NormalZ=1 AngleXU=0 Radius=6.75 StartAngle=1.5708 EndAngle=3.14159
    g5: LineSegment StartX=60 StartY=-42.5 StartZ=0 EndX=60 EndY=-41 EndZ=0
    g6: LineSegment StartX=60 StartY=-41 StartZ=0 EndX=-35.75 EndY=-41 EndZ=0
    g7: LineSegment StartX=-41 StartY=-35.75 StartZ=0 EndX=-41 EndY=35.75 EndZ=0
    g8: LineSegment StartX=-35.75 StartY=41 StartZ=0 EndX=60 EndY=41 EndZ=0
    g9: LineSegment StartX=60 StartY=41 StartZ=0 EndX=60 EndY=42.5 EndZ=0
    g10: ArcOfCircle CenterX=-35.75 CenterY=-35.75 CenterZ=0 NormalX=0 NormalY=0 NormalZ=1 AngleXU=0 Radius=5.25 StartAngle=3.14159 EndAngle=4.71239
    g11: ArcOfCircle CenterX=-35.75 CenterY=35.75 CenterZ=0 NormalX=0 NormalY=0 NormalZ=1 AngleXU=0 Radius=5.25 StartAngle=1.5708 EndAngle=3.14159
  constraints (30):
    c: Coincident(g0,g-3)
    c: Coincident(g0,g-4)
    c: Horizontal(g2)
    c: Symmetric(g2,g0,g-1)
    c: Equal(g2,g0)
    c: Coincident(g-5,g1)
    c: Coincident(g1,g-5)
    c: Coincident(g3,g2)
    c: Coincident(g3,g1)
    c: Coincident(g4,g1)
    c: Coincident(g4,g0)
    c: Equal(g4,g-4)
    c: Equal(g-4,g3)
    c: Coincident(g5,g2)
    c: Vertical(g5)
    c: Coincident(g6,g5)
    c: Horizontal(g6)
    c: Vertical(g7)
    c: Coincident(g9,g8)
    c: Coincident(g9,g0)
    c: Horizontal(g8)
    c: Vertical(g9)
    c: Equal(g5,g9)
    c: Equal(g6,g8)
    c: Tangent(g10,g6) = 1.5708
    c: Tangent(g10,g7) = 1.5708
    c: Tangent(g11,g7) = 1.5708
    c: Tangent(g11,g8) = 1.5708
    c: DistanceY(g5,g5) = 1.5
    c: Coincident(g11,g4)
FEATURE [PartDesign::Pad] Pad011
  BaseFeature = -> Pad010
  Direction = (0,0,1)
  Length = 5
  Length2 = 10
  Profile = -> Sketch015
  ReferenceAxis = -> Sketch015 [N_Axis]
  Refine = true
  Suppressed = false
  Type = 0
FEATURE [Sketcher::SketchObject] Sketch016
  ArcFitTolerance = 1e-06
  AttachmentSupport = -> [Pad011]
  ExternalGeometry = -> [Pad011]
  FullyConstrained = true
  MakeInternals = false
  MapMode = 5
  Placement = pos=(60,0,0) rot=(0.57735,0.57735,0.57735;2.0944rad)
  sketch-geometry (9):
    g0: LineSegment StartX=41.1112 StartY=6.9583 StartZ=0 EndX=45 EndY=14.5 EndZ=0
    g1: LineSegment [constr] StartX=45 StartY=14.5 StartZ=0 EndX=46.5 EndY=14.5 EndZ=0
    g2: LineSegment StartX=46.5 StartY=14.5 StartZ=0 EndX=42.6112 EndY=6.9583 EndZ=0
    g3: ArcOfCircle CenterX=43.5 CenterY=6.5 CenterZ=0 NormalX=0 NormalY=0 NormalZ=1 AngleXU=0 Radius=1 StartAngle=2.66551 EndAngle=3.14159
    g4: ArcOfCircle CenterX=42 CenterY=6.5 CenterZ=0 NormalX=0 NormalY=0 NormalZ=1 AngleXU=0 Radius=1 StartAngle=2.66551 EndAngle=3.14159
    g5: LineSegment StartX=42.5 StartY=6.5 StartZ=0 EndX=41 EndY=6.5 EndZ=0
    g6: LineSegment StartX=45 StartY=14.5 StartZ=0 EndX=45 EndY=29.5 EndZ=0
    g7: LineSegment StartX=45 StartY=29.5 StartZ=0 EndX=46.5 EndY=29.5 EndZ=0
    g8: LineSegment StartX=46.5 StartY=29.5 StartZ=0 EndX=46.5 EndY=14.5 EndZ=0
  constraints (24):
    c: Coincident(g0,g1)
    c: Horizontal(g1)
    c: Coincident(g1,g2)
    c: Coincident(g3,g-3)
    c: Coincident(g4,g-3)
    c: Tangent(g4,g0) = 1.5708
    c: Tangent(g3,g2) = -1.5708
    c: Coincident(g5,g3)
    c: Coincident(g5,g4)
    c: Perpendicular(g3,g5)
    c: Perpendicular(g4,g5)
    c: Equal(g1,g5)
    c: Radius(g4) = 1
    c: DistanceY(g3,g1) = 8
    c: DistanceX(g3,g1) = 4
    c: Equal(g4,g3)
    c: Coincident(g0,g6)
    c: Vertical(g6)
    c: Coincident(g6,g7)
    c: Horizontal(g7)
    c: Coincident(g7,g8)
    c: Coincident(g8,g1)
    c: Vertical(g8)
    c: DistanceY(g8,g8) = 15
FEATURE [PartDesign::AdditivePipe] AdditivePipe001
  AuxilleryCurvelinear = true
  AuxillerySpineTangent = false
  BaseFeature = -> Pad011
  Binormal = (0,0,0)
  Mode = 0
  Profile = -> Sketch016
  Refine = true
  Spine = -> Pad011 [Edge32,Edge33,Edge34,Edge35,Edge36]
  SpineTangent = false
  Suppressed = false
  Transformation = 0
  Transition = 0
FEATURE [Sketcher::SketchObject] Sketch017
  ArcFitTolerance = 1e-06
  AttachmentSupport = -> [XY_Plane004]
  ExternalGeometry = -> [AdditivePipe001]
  FullyConstrained = true
  MakeInternals = false
  MapMode = 5
  sketch-geometry (5):
    g0: LineSegment StartX=-30.75 StartY=42.5 StartZ=0 EndX=-30.75 EndY=-42.5 EndZ=0
    g1: LineSegment StartX=-30.75 StartY=-42.5 StartZ=0 EndX=-29.25 EndY=-42.5 EndZ=0
    g2: LineSegment StartX=-29.25 StartY=-42.5 StartZ=0 EndX=-29.25 EndY=42.5 EndZ=0
    g3: LineSegment StartX=-29.25 StartY=42.5 StartZ=0 EndX=-30.75 EndY=42.5 EndZ=0
    g4: GeomPoint [constr] X=-30 Y=0 Z=0
  constraints (13):
    c: Coincident(g0,g1)
    c: Coincident(g1,g2)
    c: Coincident(g2,g3)
    c: Coincident(g3,g0)
    c: Vertical(g0)
    c: Vertical(g2)
    c: Horizontal(g1)
    c: Horizontal(g3)
    c: Symmetric(g2,g0,g4)
    c: PointOnObject(g4,g-1)
    c: PointOnObject(g1,g-3)
    c: DistanceX(g3,g3) = 1.5
    c: DistanceX(g4,g-1) = 30
FEATURE [PartDesign::Pad] Pad012
  BaseFeature = -> AdditivePipe001
  Direction = (0,0,1)
  Length = 10
  Length2 = 10
  Profile = -> Sketch017
  ReferenceAxis = -> Sketch017 [N_Axis]
  Refine = true
  Suppressed = false
  Type = 3
  UpToFace = -> AdditivePipe001 [Face4]
FEATURE [PartDesign::LinearPattern] LinearPattern004
  BaseFeature = -> Pad012
  Direction = -> Sketch017 [H_Axis]
  Length = 60
  Mode = 0
  Occurrences = 5
  Offset = 15
  Originals = -> [Pad012]
  Refine = true
  Suppressed = false
  TransformMode = 0
FEATURE [Sketcher::SketchObject] Sketch018
  ArcFitTolerance = 1e-06
  AttachmentSupport = -> [XY_Plane004]
  ExternalGeometry = -> [LinearPattern004]
  FullyConstrained = true
  MakeInternals = false
  MapMode = 5
  sketch-geometry (5):
    g0: LineSegment StartX=42.5 StartY=29.25 StartZ=0 EndX=42.5 EndY=30.75 EndZ=0
    g1: LineSegment StartX=42.5 StartY=30.75 StartZ=0 EndX=-42.5 EndY=30.75 EndZ=0
    g2: LineSegment StartX=-42.5 StartY=30.75 StartZ=0 EndX=-42.5 EndY=29.25 EndZ=0
    g3: LineSegment StartX=-42.5 StartY=29.25 StartZ=0 EndX=42.5 EndY=29.25 EndZ=0
    g4: GeomPoint [constr] X=0 Y=30 Z=0
  constraints (13):
    c: Coincident(g0,g1)
    c: Coincident(g1,g2)
    c: Coincident(g2,g3)
    c: Coincident(g3,g0)
    c: Vertical(g0)
    c: Vertical(g2)
    c: Horizontal(g1)
    c: Horizontal(g3)
    c: Symmetric(g2,g0,g4)
    c: PointOnObject(g4,g-2)
    c: PointOnObject(g1,g-3)
    c: DistanceY(g4) = 30
    c: DistanceY(g0,g0) = 1.5
FEATURE [PartDesign::Pad] Pad013
  BaseFeature = -> LinearPattern004
  Direction = (0,0,1)
  Length = 10
  Length2 = 10
  Profile = -> Sketch018
  ReferenceAxis = -> Sketch018 [N_Axis]
  Refine = true
  Suppressed = false
  Type = 3
  UpToFace = -> LinearPattern004 [Face68]
FEATURE [PartDesign::LinearPattern] LinearPattern005
  BaseFeature = -> Pad013
  Direction = -> Sketch018 [V_Axis]
  Length = 60
  Mode = 0
  Occurrences = 5
  Offset = 15
  Originals = -> [Pad013]
  Refine = true
  Reversed = true
  Suppressed = false
  TransformMode = 0
FEATURE [PartDesign::CoordinateSystem] FanMountHole001
  AttacherType = Attacher::AttachEngine3D
  AttachmentSupport = -> [LinearPattern005]
  MapMode = 11
  Placement = pos=(-35.75,-35.75,0) rot=(0,0,1;1.5708rad)
FEATURE [Sketcher::SketchObject] Sketch019
  ArcFitTolerance = 1e-06
  AttachmentSupport = -> [XZ_Plane004]
  ExternalGeometry = -> [LinearPattern005]
  FullyConstrained = true
  MakeInternals = false
  MapMode = 5
  Placement = pos=(0,0,0) rot=(1,0,0;1.5708rad)
  sketch-geometry (4):
    g0: LineSegment StartX=60 StartY=29.5 StartZ=0 EndX=60 EndY=0 EndZ=0
    g1: LineSegment StartX=60 StartY=0 StartZ=0 EndX=43 EndY=0 EndZ=0
    g2: LineSegment StartX=43 StartY=0 StartZ=0 EndX=37.7984 EndY=29.5 EndZ=0
    g3: LineSegment StartX=37.7984 StartY=29.5 StartZ=0 EndX=60 EndY=29.5 EndZ=0
  constraints (11):
    c: PointOnObject(g0,g-1)
    c: Vertical(g0)
    c: Coincident(g0,g1)
    c: PointOnObject(g1,g-1)
    c: Coincident(g1,g2)
    c: Coincident(g2,g3)
    c: Coincident(g3,g0)
    c: DistanceX(g-1,g1) = 43
    c: Angle(g1,g2) = 1.74533
    c: Coincident(g0,g-3)
    c: PointOnObject(g2,g-3)
FEATURE [PartDesign::Pocket] Pocket002
  BaseFeature = -> LinearPattern005
  Direction = (0,1,-2e-16)
  Length = 5
  Length2 = 5
  Midplane = true
  Profile = -> Sketch019
  ReferenceAxis = -> Sketch019 [N_Axis]
  Refine = true
  Suppressed = false
  Type = 1
FEATURE [PartDesign::CoordinateSystem] FilterHolderMount001
  AttacherType = Attacher::AttachEngine3D
  AttachmentSupport = -> [Pocket002]
  MapMode = 11
  Placement = pos=(-35.75,35.75,1.5) rot=(0,0,1;1.5708rad)
FEATURE [PartDesign::CoordinateSystem] OtherFanHolder001
  AttacherType = Attacher::AttachEngine3D
  AttachmentSupport = -> [Pocket002]
  MapMode = 45
  Placement = pos=(42.8701,0,0.736527) rot=(0.642788,0,0.766044;3.14159rad)
FEATURE [Sketcher::SketchObject] Sketch022
  ArcFitTolerance = 1e-06
  FullyConstrained = true
  MakeInternals = false
  MapMode = 5
  Placement = pos=(41.7034,1.6e-15,7.35343) rot=(0.540716,0.540716,0.6444;1.99673rad)
  sketch-geometry (6):
    g0: ArcOfCircle CenterX=43.0908 CenterY=-0.761797 CenterZ=0 NormalX=0 NormalY=0 NormalZ=1 AngleXU=0 Radius=0.6 StartAngle=2.49691 EndAngle=3.31716
    g1: LineSegment StartX=44.66 StartY=3.6334 StartZ=0 EndX=42.6112 EndY=-0.401229 EndZ=0
    g2: LineSegment StartX=42.5 StartY=-5.3666 StartZ=0 EndX=42.5 EndY=-0.866599 EndZ=0
    g3: LineSegment StartX=42.5 StartY=-5.3666 StartZ=0 EndX=50.5 EndY=-5.3666 EndZ=0
    g4: LineSegment StartX=44.66 StartY=3.6334 StartZ=0 EndX=50.5 EndY=3.6334 EndZ=0
    g5: ArcOfCircle CenterX=50.5 CenterY=-0.866599 CenterZ=0 NormalX=0 NormalY=0 NormalZ=1 AngleXU=0 Radius=4.5 StartAngle=4.71239 EndAngle=7.85398
  constraints (16):
    c: Coincident(g0,g-3)
    c: Coincident(g0,g-4)
    c: Radius(g0) = 0.6
    c: Coincident(g3,g2)
    c: Horizontal(g3)
    c: Coincident(g4,g1)
    c: Horizontal(g4)
    c: Diameter(g5) = 9
    c: PointOnObject(g1,g-4)
    c: Horizontal(g5,g2)
    c: Tangent(g5,g3) = -1.5708
    c: Tangent(g5,g4) = 1.5708
    c: DistanceX(g-4,g5) = 4
    c: Coincident(g2,g0)
    c: Coincident(g0,g1)
    c: PointOnObject(g2,g-3)
FEATURE [PartDesign::Pocket] Pocket003
  BaseFeature = -> Pocket002
  Direction = (-0.984808,2e-16,-0.173648)
  Length = 50
  Length2 = 5
  Midplane = true
  Profile = -> Sketch022
  ReferenceAxis = -> Sketch022 [N_Axis]
  Refine = true
  Suppressed = false
  Type = 0
FEATURE [PartDesign::Body] Body003  label="Fan2Holder"
  AllowCompound = false
  Group = -> [Sketch014,Pad010,Sketch015,Pad011,Sketch016,AdditivePipe001,Sketch017,Pad012,LinearPattern004,Sketch018,Pad013,LinearPattern005,FanMountHole001,Sketch019,Pocket002,OtherFanHolder001,FilterHolderMount001,Sketch022,Pocket003]
  Origin = -> Origin004
  Tip = -> Pocket003
FEATURE [Sketcher::SketchObject] Sketch023
  ArcFitTolerance = 1e-06
  AttachmentSupport = -> [XY_Plane003]
  FullyConstrained = true
  MakeInternals = false
  MapMode = 5
  sketch-geometry (10):
    g0: LineSegment StartX=-55 StartY=25 StartZ=0 EndX=-55 EndY=-25 EndZ=0
    g1: LineSegment StartX=-45 StartY=-35 StartZ=0 EndX=45 EndY=-35 EndZ=0
    g2: LineSegment StartX=55 StartY=-25 StartZ=0 EndX=55 EndY=25 EndZ=0
    g3: LineSegment StartX=45 StartY=35 StartZ=0 EndX=-45 EndY=35 EndZ=0
    g4: ArcOfCircle CenterX=-45 CenterY=25 CenterZ=0 NormalX=0 NormalY=0 NormalZ=1 AngleXU=0 Radius=10 StartAngle=1.5708 EndAngle=3.14159
    g5: ArcOfCircle CenterX=-45 CenterY=-25 CenterZ=0 NormalX=0 NormalY=0 NormalZ=1 AngleXU=0 Radius=10 StartAngle=3.14159 EndAngle=4.71239
    g6: ArcOfCircle CenterX=45 CenterY=-25 CenterZ=0 NormalX=0 NormalY=0 NormalZ=1 AngleXU=0 Radius=10 StartAngle=4.71239 EndAngle=6.28319
    g7: ArcOfCircle CenterX=45 CenterY=25 CenterZ=0 NormalX=0 NormalY=0 NormalZ=1 AngleXU=0 Radius=10 StartAngle=1e-16 EndAngle=1.5708
    g8: GeomPoint [constr] X=-55 Y=35 Z=0
    g9: GeomPoint [constr] X=55 Y=-35 Z=0
  constraints (22):
    c: Tangent(g0,g4) = -1.5708
    c: Tangent(g0,g5) = -1.5708
    c: Tangent(g1,g5) = -1.5708
    c: Tangent(g1,g6) = -1.5708
    c: Tangent(g2,g6) = -1.5708
    c: Tangent(g2,g7) = -1.5708
    c: Tangent(g3,g7) = -1.5708
    c: Tangent(g3,g4) = -1.5708
    c: Vertical(g2)
    c: Horizontal(g1)
    c: Equal(g4,g5)
    c: Equal(g5,g6)
    c: Equal(g6,g7)
    c: PointOnObject(g8,g0)
    c: PointOnObject(g8,g3)
    c: PointOnObject(g9,g1)
    c: PointOnObject(g9,g2)
    c: Symmetric(g3,g3,g-2)
    c: Symmetric(g0,g0,g-1)
    c: DistanceX(g0,g2) = 110
    c: DistanceY(g1,g3) = 70
    c: Radius(g7) = 10
FEATURE [PartDesign::Pad] Pad014
  Direction = (0,0,1)
  Length = 20
  Length2 = 10
  Profile = -> Sketch023
  ReferenceAxis = -> Sketch023 [N_Axis]
  Refine = true
  Suppressed = false
  Type = 0
FEATURE [Sketcher::SketchObject] Sketch024
  ArcFitTolerance = 1e-06
  AttachmentSupport = -> [XZ_Plane003]
  ExternalGeometry = -> [Pad014]
  FullyConstrained = true
  MakeInternals = false
  MapMode = 5
  Placement = pos=(0,0,0) rot=(1,0,0;1.5708rad)
  sketch-geometry (5):
    g0: LineSegment StartX=55 StartY=20 StartZ=0 EndX=45 EndY=20 EndZ=0
    g1: ArcOfCircle CenterX=45 CenterY=16 CenterZ=0 NormalX=0 NormalY=0 NormalZ=1 AngleXU=0 Radius=4 StartAngle=0.413862 EndAngle=1.5708
    g2: ArcOfCircle CenterX=47 CenterY=1.5 CenterZ=0 NormalX=0 NormalY=0 NormalZ=1 AngleXU=0 Radius=8 StartAngle=3e-16 EndAngle=0.413862
    g3: LineSegment StartX=54.3246 StartY=4.71719 StartZ=0 EndX=48.6623 EndY=17.6086 EndZ=0
    g4: LineSegment StartX=55 StartY=20 StartZ=0 EndX=55 EndY=1.5 EndZ=0
  constraints (12):
    c: Horizontal(g0)
    c: Tangent(g1,g0) = -1.5708
    c: Tangent(g3,g2) = -1.5708
    c: Tangent(g3,g1) = -1.5708
    c: Coincident(g0,g-3)
    c: Coincident(g4,g0)
    c: PointOnObject(g4,g-3)
    c: Tangent(g4,g2) = 1.5708
    c: DistanceY(g2) = 1.5
    c: DistanceX(g0,g0) = 10
    c: Radius(g2) = 8
    c: Radius(g1) = 4
FEATURE [PartDesign::SubtractivePipe] SubtractivePipe
  AuxilleryCurvelinear = true
  AuxillerySpineTangent = false
  BaseFeature = -> Pad014
  Binormal = (0,0,0)
  Mode = 0
  Profile = -> Sketch024
  Refine = true
  Spine = -> Pad014 [Edge16,Edge19,Edge22,Edge24,Edge4,Edge7,Edge10,Edge13]
  SpineTangent = false
  Suppressed = false
  Transformation = 0
  Transition = 0
FEATURE [Sketcher::SketchObject] Sketch025
  ArcFitTolerance = 1e-06
  AttachmentSupport = -> [YZ_Plane003]
  ExternalGeometry = -> [SubtractivePipe]
  FullyConstrained = true
  MakeInternals = false
  MapMode = 5
  Placement = pos=(0,0,0) rot=(0.57735,0.57735,0.57735;2.0944rad)
  sketch-geometry (7):
    g0: LineSegment StartX=-7.5 StartY=20 StartZ=0 EndX=7.5 EndY=20 EndZ=0
    g1: ArcOfCircle CenterX=7.5 CenterY=23 CenterZ=0 NormalX=0 NormalY=0 NormalZ=1 AngleXU=0 Radius=3 StartAngle=3.14159 EndAngle=4.71239
    g2: ArcOfCircle CenterX=-7.5 CenterY=23 CenterZ=0 NormalX=0 NormalY=0 NormalZ=1 AngleXU=0 Radius=3 StartAngle=4.71239 EndAngle=6.28319
    g3: ArcOfCircle CenterX=8.84e-14 CenterY=28 CenterZ=0 NormalX=0 NormalY=0 NormalZ=1 AngleXU=0 Radius=4.5 StartAngle=-6.7475e-12 EndAngle=3.14159
    g4: LineSegment StartX=4.5 StartY=23 StartZ=0 EndX=4.5 EndY=28 EndZ=0
    g5: LineSegment StartX=-4.5 StartY=23 StartZ=0 EndX=-4.5 EndY=28 EndZ=0
    g6: Circle CenterX=8.84e-14 CenterY=28 CenterZ=0 NormalX=0 NormalY=0 NormalZ=1 AngleXU=0 Radius=2.75
  constraints (16):
    c: PointOnObject(g0,g-3)
    c: Symmetric(g0,g0,g-2)
    c: Vertical(g5)
    c: Tangent(g4,g3) = -1.5708
    c: Tangent(g4,g1) = 1.5708
    c: Tangent(g1,g0) = -1.5708
    c: Tangent(g2,g0) = -1.5708
    c: Tangent(g5,g2) = -1.5708
    c: Tangent(g5,g3) = 1.5708
    c: Vertical(g4)
    c: Equal(g1,g2)
    c: Diameter(g3) = 9
    c: Coincident(g6,g3)
    c: Diameter(g6) = 5.5
    c: Radius(g1) = 3
    c: DistanceY(g0,g3) = 8
FEATURE [PartDesign::Pad] Pad015
  BaseFeature = -> SubtractivePipe
  Direction = (1,0,0)
  Length = 70
  Length2 = 10
  Midplane = true
  Profile = -> Sketch025
  ReferenceAxis = -> Sketch025 [N_Axis]
  Refine = true
  Suppressed = false
  Type = 0
FEATURE [Sketcher::SketchObject] Sketch026
  ArcFitTolerance = 1e-06
  AttachmentSupport = -> [XZ_Plane003]
  ExternalGeometry = -> [Pad015]
  FullyConstrained = true
  MakeInternals = false
  MapMode = 5
  Placement = pos=(0,0,0) rot=(1,0,0;1.5708rad)
  sketch-geometry (5):
    g0: LineSegment StartX=-25.5 StartY=35 StartZ=0 EndX=-25.5 EndY=20 EndZ=0
    g1: LineSegment StartX=-25.5 StartY=20 StartZ=0 EndX=25.5 EndY=20 EndZ=0
    g2: LineSegment StartX=25.5 StartY=20 StartZ=0 EndX=25.5 EndY=35 EndZ=0
    g3: LineSegment StartX=25.5 StartY=35 StartZ=0 EndX=-25.5 EndY=35 EndZ=0
    g4: GeomPoint [constr] X=0 Y=27.5 Z=0
  constraints (13):
    c: Coincident(g0,g1)
    c: Coincident(g1,g2)
    c: Coincident(g2,g3)
    c: Coincident(g3,g0)
    c: Vertical(g0)
    c: Vertical(g2)
    c: Horizontal(g1)
    c: Horizontal(g3)
    c: Symmetric(g2,g0,g4)
    c: PointOnObject(g4,g-2)
    c: PointOnObject(g1,g-3)
    c: DistanceX(g3,g3) = 51
    c: DistanceY(g2,g2) = 15
FEATURE [PartDesign::Pocket] Pocket004
  BaseFeature = -> Pad015
  Direction = (0,1,-2e-16)
  Length = 5
  Length2 = 5
  Midplane = true
  Profile = -> Sketch026
  ReferenceAxis = -> Sketch026 [N_Axis]
  Refine = true
  Suppressed = false
  Type = 1
FEATURE [Sketcher::SketchObject] Sketch027
  ArcFitTolerance = 1e-06
  AttachmentSupport = -> [Pocket004]
  ExternalGeometry = -> [Pocket004]
  FullyConstrained = true
  MakeInternals = false
  MapMode = 5
  Placement = pos=(0,-30.5104,13.4011) rot=(1,0,0;1.15693rad)
  sketch-geometry (5):
    g0: LineSegment StartX=-34.25 StartY=0 StartZ=0 EndX=-34.25 EndY=-4 EndZ=0
    g1: LineSegment StartX=-34.25 StartY=-4 StartZ=0 EndX=-26.25 EndY=-4 EndZ=0
    g2: LineSegment StartX=-26.25 StartY=-4 StartZ=0 EndX=-26.25 EndY=0 EndZ=0
    g3: LineSegment StartX=-26.25 StartY=0 StartZ=0 EndX=-34.25 EndY=0 EndZ=0
    g4: LineSegment [constr] StartX=-30.25 StartY=0 StartZ=0 EndX=-30.25 EndY=15.2954 EndZ=0
  constraints (14):
    c: Coincident(g0,g1)
    c: Coincident(g1,g2)
    c: Coincident(g2,g3)
    c: Coincident(g3,g0)
    c: Vertical(g0)
    c: Vertical(g2)
    c: Horizontal(g1)
    c: Horizontal(g3)
    c: PointOnObject(g0,g-1)
    c: DistanceY(g2,g2) = 4
    c: DistanceX(g1,g1) = 8
    c: Symmetric(g3,g3,g4)
    c: Vertical(g4)
    c: Symmetric(g-3,g-3,g4)
FEATURE [PartDesign::Pocket] Pocket005
  BaseFeature = -> Pocket004
  Direction = (0,0.915575,-0.402148)
  Length = 10
  Length2 = 5
  Profile = -> Sketch027
  ReferenceAxis = -> Sketch027 [N_Axis]
  Refine = true
  Suppressed = false
  Type = 0
FEATURE [Sketcher::SketchObject] Sketch028
  ArcFitTolerance = 1e-06
  AttachmentSupport = -> [Pocket005]
  ExternalGeometry = -> [Pocket005]
  FullyConstrained = true
  MakeInternals = false
  MapMode = 5
  Placement = pos=(-2.8e-15,35,0) rot=(0,0.707107,0.707107;3.14159rad)
  sketch-geometry (6):
    g0: LineSegment StartX=24.25 StartY=15.1629 StartZ=0 EndX=24.25 EndY=7.16289 EndZ=0
    g1: LineSegment StartX=24.25 StartY=7.16289 StartZ=0 EndX=36.25 EndY=7.16289 EndZ=0
    g2: LineSegment StartX=36.25 StartY=7.16289 StartZ=0 EndX=36.25 EndY=15.1629 EndZ=0
    g3: LineSegment StartX=36.25 StartY=15.1629 StartZ=0 EndX=24.25 EndY=15.1629 EndZ=0
    g4: LineSegment [constr] StartX=30.25 StartY=15.1629 StartZ=0 EndX=30.25 EndY=23 EndZ=0
    g5: LineSegment [constr] StartX=45 StartY=11.1629 StartZ=0 EndX=36.25 EndY=11.1629 EndZ=0
  constraints (16):
    c: Coincident(g0,g1)
    c: Coincident(g1,g2)
    c: Coincident(g2,g3)
    c: Coincident(g3,g0)
    c: Vertical(g0)
    c: Vertical(g2)
    c: Horizontal(g1)
    c: Horizontal(g3)
    c: Symmetric(g3,g3,g4)
    c: Symmetric(g-3,g-3,g4)
    c: Vertical(g4)
    c: DistanceX(g3,g3) = 12
    c: DistanceY(g2,g2) = 8
    c: Symmetric(g-4,g-4,g5)
    c: Symmetric(g2,g2,g5)
    c: Horizontal(g5)
FEATURE [PartDesign::Pocket] Pocket006
  BaseFeature = -> Pocket005
  Direction = (0,-1,2e-16)
  Length = 63
  Length2 = 5
  Profile = -> Sketch028
  ReferenceAxis = -> Sketch028 [N_Axis]
  Refine = true
  Suppressed = false
  Type = 0
FEATURE [Sketcher::SketchObject] Sketch029
  ArcFitTolerance = 1e-06
  AttachmentSupport = -> [Pocket006]
  ExternalGeometry = -> [Pocket006]
  FullyConstrained = true
  MakeInternals = false
  MapMode = 5
  Placement = pos=(0,0,0) rot=(1,0,0;3.14159rad)
  sketch-geometry (10):
    g0: LineSegment StartX=-45 StartY=20 StartZ=0 EndX=-45 EndY=-20 EndZ=0
    g1: LineSegment StartX=-40 StartY=-25 StartZ=0 EndX=40 EndY=-25 EndZ=0
    g2: LineSegment StartX=45 StartY=-20 StartZ=0 EndX=45 EndY=20 EndZ=0
    g3: LineSegment StartX=40 StartY=25 StartZ=0 EndX=-40 EndY=25 EndZ=0
    g4: ArcOfCircle CenterX=-40 CenterY=20 CenterZ=0 NormalX=0 NormalY=0 NormalZ=1 AngleXU=0 Radius=5 StartAngle=1.5708 EndAngle=3.14159
    g5: ArcOfCircle CenterX=-40 CenterY=-20 CenterZ=0 NormalX=0 NormalY=0 NormalZ=1 AngleXU=0 Radius=5 StartAngle=3.14159 EndAngle=4.71239
    g6: ArcOfCircle CenterX=40 CenterY=-20 CenterZ=0 NormalX=0 NormalY=0 NormalZ=1 AngleXU=0 Radius=5 StartAngle=4.71239 EndAngle=6.28319
    g7: ArcOfCircle CenterX=40 CenterY=20 CenterZ=0 NormalX=0 NormalY=0 NormalZ=1 AngleXU=0 Radius=5 StartAngle=9.685e-13 EndAngle=1.5708
    g8: GeomPoint [constr] X=-45 Y=25 Z=0
    g9: GeomPoint [constr] X=45 Y=-25 Z=0
  constraints (22):
    c: Tangent(g0,g4) = -1.5708
    c: Tangent(g0,g5) = -1.5708
    c: Tangent(g1,g5) = -1.5708
    c: Tangent(g1,g6) = -1.5708
    c: Tangent(g2,g6) = -1.5708
    c: Tangent(g2,g7) = -1.5708
    c: Tangent(g3,g7) = -1.5708
    c: Tangent(g3,g4) = -1.5708
    c: Vertical(g2)
    c: Horizontal(g1)
    c: Equal(g4,g5)
    c: Equal(g5,g6)
    c: Equal(g6,g7)
    c: PointOnObject(g8,g0)
    c: PointOnObject(g8,g3)
    c: PointOnObject(g9,g1)
    c: PointOnObject(g9,g2)
    c: Radius(g5) = 5
    c: Symmetric(g3,g3,g-2)
    c: Symmetric(g0,g0,g-1)
    c: DistanceX(g2,g-3) = 10
    c: DistanceY(g3,g-4) = 10
FEATURE [PartDesign::Pocket] Pocket007
  BaseFeature = -> Pocket006
  Direction = (0,0,1)
  Length = 15
  Length2 = 5
  Profile = -> Sketch029
  ReferenceAxis = -> Sketch029 [N_Axis]
  Refine = true
  Suppressed = false
  Type = 0
FEATURE [PartDesign::CoordinateSystem] Fan  label="FanHolders"
  AttacherType = Attacher::AttachEngine3D
  AttachmentSupport = -> [Pocket007]
  MapMode = 45
  Placement = pos=(0,1.014e-13,28) rot=(0.57735,0.57735,0.57735;2.0944rad)
FEATURE [PartDesign::CoordinateSystem] Bottom
  AttacherType = Attacher::AttachEngine3D
  AttachmentSupport = -> [Pocket007]
  MapMode = 45
  Placement = pos=(-2.3879e-12,-1.227e-13,0) rot=(0,0,1;1.5708rad)
FEATURE [PartDesign::Body] Body002  label="Base"
  AllowCompound = false
  Group = -> [Sketch023,Pad014,Sketch024,SubtractivePipe,Sketch025,Pad015,Sketch026,Pocket004,Sketch027,Pocket005,Sketch028,Pocket006,Sketch029,Pocket007,Fan,Bottom]
  Origin = -> Origin003
  Tip = -> Pocket007
FEATURE [Sketcher::SketchObject] Sketch030
  ArcFitTolerance = 1e-06
  AttachmentSupport = -> [XY_Plane005]
  FullyConstrained = true
  MakeInternals = false
  MapMode = 5
  sketch-geometry (10):
    g0: LineSegment StartX=-55 StartY=25 StartZ=0 EndX=-55 EndY=-25 EndZ=0
    g1: LineSegment StartX=-45 StartY=-35 StartZ=0 EndX=45 EndY=-35 EndZ=0
    g2: LineSegment StartX=55 StartY=-25 StartZ=0 EndX=55 EndY=25 EndZ=0
    g3: LineSegment StartX=45 StartY=35 StartZ=0 EndX=-45 EndY=35 EndZ=0
    g4: ArcOfCircle CenterX=-45 CenterY=25 CenterZ=0 NormalX=0 NormalY=0 NormalZ=1 AngleXU=0 Radius=10 StartAngle=1.5708 EndAngle=3.14159
    g5: ArcOfCircle CenterX=-45 CenterY=-25 CenterZ=0 NormalX=0 NormalY=0 NormalZ=1 AngleXU=0 Radius=10 StartAngle=3.14159 EndAngle=4.71239
    g6: ArcOfCircle CenterX=45 CenterY=-25 CenterZ=0 NormalX=0 NormalY=0 NormalZ=1 AngleXU=0 Radius=10 StartAngle=4.71239 EndAngle=6.28319
    g7: ArcOfCircle CenterX=45 CenterY=25 CenterZ=0 NormalX=0 NormalY=0 NormalZ=1 AngleXU=0 Radius=10 StartAngle=0 EndAngle=1.5708
    g8: GeomPoint [constr] X=-55 Y=35 Z=0
    g9: GeomPoint [constr] X=55 Y=-35 Z=0
  constraints (22):
    c: Tangent(g0,g4) = -1.5708
    c: Tangent(g0,g5) = -1.5708
    c: Tangent(g1,g5) = -1.5708
    c: Tangent(g1,g6) = -1.5708
    c: Tangent(g2,g6) = -1.5708
    c: Tangent(g2,g7) = -1.5708
    c: Tangent(g3,g7) = -1.5708
    c: Tangent(g3,g4) = -1.5708
    c: Vertical(g2)
    c: Horizontal(g1)
    c: Equal(g4,g5)
    c: Equal(g5,g6)
    c: Equal(g6,g7)
    c: PointOnObject(g8,g0)
    c: PointOnObject(g8,g3)
    c: PointOnObject(g9,g1)
    c: PointOnObject(g9,g2)
    c: Radius(g5) = 10
    c: Symmetric(g3,g3,g-2)
    c: Symmetric(g0,g0,g-1)
    c: DistanceX(g0,g2) = 110
    c: DistanceY(g1,g3) = 70
FEATURE [App::Link] Base  label="Base001"
  AttachedBy = #Bottom
  AttachedTo = Parent Assembly#LCS_Origin
  AttachmentOffset = pos=(0,0,0) rot=(0,0,1;1.5708rad)
  LinkPlacement = pos=(2.3879e-12,1.227e-13,0) rot=(0,0,1;0rad)
  LinkedObject = -> Body002
  Placement = pos=(2.3879e-12,1.227e-13,0) rot=(0,0,1;0rad)
  SolverId = Asm4EE
  expr: Placement = LCS_Origin.Placement * AttachmentOffset * Bottom.Placement ^ -1
FEATURE [App::Link] Fan1Holder  label="Fan1Holder001"
  AttachedBy = #Mount1
  AttachedTo = Base#Fan
  AttachmentOffset = pos=(0,0,0) rot=(0.707107,-0.707107,0;3.14159rad)
  LinkPlacement = pos=(2.3343e-12,6.5,78.5) rot=(-0.57735,0.57735,-0.57735;4.18879rad)
  LinkedObject = -> Body
  Placement = pos=(2.3343e-12,6.5,78.5) rot=(-0.57735,0.57735,-0.57735;4.18879rad)
  SolverId = Asm4EE
  expr: Placement = Base.Placement * Fan.Placement * AttachmentOffset * Mount1.Placement ^ -1
FEATURE [App::Link] Fan2Holder  label="Fan2Holder001"
  AttachedBy = #OtherFanHolder001
  AttachedTo = Fan1Holder#OtherFanHolder
  AttachmentOffset = pos=(0,0,0) rot=(1,0,0;3.14159rad)
  LinkPlacement = pos=(2.4492e-12,-8.20687,161.907) rot=(0.633687,0.633687,-0.443713;2.30637rad)
  LinkedObject = -> Body003
  Placement = pos=(2.4492e-12,-8.20687,161.907) rot=(0.633687,0.633687,-0.443713;2.30637rad)
  SolverId = Asm4EE
  expr: Placement = Fan1Holder.Placement * OtherFanHolder.Placement * AttachmentOffset * OtherFanHolder001.Placement ^ -1
FEATURE [App::Link] FilterHolder  label="FilterHolder001"
  AttachedBy = #FanHolder
  AttachedTo = Fan1Holder#FilterHolderMount
  AttachmentOffset = pos=(0,0,0) rot=(-0.707107,-0.707107,0;3.14159rad)
  LinkPlacement = pos=(2.3874e-12,0.5,78.5) rot=(-1,0,0;1.5708rad)
  LinkedObject = -> Body001
  Placement = pos=(2.3874e-12,0.5,78.5) rot=(-1,0,0;1.5708rad)
  SolverId = Asm4EE
  expr: Placement = Fan1Holder.Placement * FilterHolderMount.Placement * AttachmentOffset * FanHolder.Placement ^ -1
FEATURE [App::Link] FilterHolder001  label="FilterHolder002"
  AttachedBy = #FanHolder
  AttachedTo = Fan2Holder#FilterHolderMount001
  AttachmentOffset = pos=(0,0,0) rot=(-0.707107,-0.707107,0;3.14159rad)
  LinkPlacement = pos=(2.4869e-12,-13.845,159.855) rot=(0,-0.573576,-0.819152;3.14159rad)
  LinkedObject = -> Body001
  Placement = pos=(2.4869e-12,-13.845,159.855) rot=(0,-0.573576,-0.819152;3.14159rad)
  SolverId = Asm4EE
  expr: Placement = Fan2Holder.Placement * FilterHolderMount001.Placement * AttachmentOffset * FanHolder.Placement ^ -1
FEATURE [App::Link] _0mmAxialFan  label="80mmAxialFan"
  AttachedBy = #FanHouse_TopMountHole
  AttachedTo = Fan1Holder#FanMountHole
  AttachmentOffset = pos=(0,0,0) rot=(0,0,1;1.5708rad)
  LinkPlacement = pos=(2.1458e-12,31.5,78.5) rot=(0,0.707107,-0.707107;3.14159rad)
  LinkedObject = -> <external Axial Fan.FCStd>#Assembly
  Placement = pos=(2.1458e-12,31.5,78.5) rot=(0,0.707107,-0.707107;3.14159rad)
  SolverId = Asm4EE
  expr: Placement = Fan1Holder.Placement * FanMountHole.Placement * AttachmentOffset * Axial_Fan#FanHouse_TopMountHole.Placement ^ -1
FEATURE [App::Link] _0mmAxialFan001  label="80mmAxialFan001"
  AttachedBy = #FanHouse_TopMountHole
  AttachedTo = Fan2Holder#FanMountHole001
  AttachmentOffset = pos=(0,0,0) rot=(0,0,1;1.5708rad)
  LinkPlacement = pos=(2.2737e-12,15.2854,170.457) rot=(1,0,0;1.91986rad)
  LinkedObject = -> <external Axial Fan.FCStd>#Assembly
  Placement = pos=(2.2737e-12,15.2854,170.457) rot=(1,0,0;1.91986rad)
  SolverId = Asm4EE
  expr: Placement = Fan2Holder.Placement * FanMountHole001.Placement * AttachmentOffset * Axial_Fan#FanHouse_TopMountHole.Placement ^ -1
FEATURE [App::Link] BottomCover  label="BottomCover001"
  AttachedBy = #Base001
  AttachedTo = Base#Bottom
  LinkPlacement = pos=(8.91e-14,6.93e-14,-1.5) rot=(0,0,1;0rad)
  LinkedObject = -> Body004
  Placement = pos=(8.91e-14,6.93e-14,-1.5) rot=(0,0,1;0rad)
  SolverId = Asm4EE
  expr: Placement = Base.Placement * Bottom.Placement * AttachmentOffset * Base001.Placement ^ -1
FEATURE [PartDesign::Pad] Pad016
  Direction = (0,0,1)
  Length = 1.5
  Length2 = 10
  Profile = -> Sketch030
  ReferenceAxis = -> Sketch030 [N_Axis]
  Refine = true
  Suppressed = false
  Type = 0
FEATURE [PartDesign::CoordinateSystem] Base001  label="Base002"
  AttacherType = Attacher::AttachEngine3D
  AttachmentSupport = -> [Pad016]
  MapMode = 45
  Placement = pos=(-8.91e-14,-6.93e-14,1.5) rot=(0,0,1;1.5708rad)
FEATURE [PartDesign::Body] Body004  label="BottomCover"
  AllowCompound = false
  Group = -> [Sketch030,Base001,Pad016]
  Origin = -> Origin005
  Tip = -> Pad016
FEATURE [App::Link] Base002  label="Base003"
  AttachedBy = #Fan
  AttachedTo = Fan1Holder#Mount2
  AttachmentOffset = pos=(0,0,0) rot=(0,0,1;4.71239rad)
  LinkPlacement = pos=(50.5,27.5746,125.216) rot=(0.60812,-0.60812,0.510274;2.19793rad)
  LinkedObject = -> Body002
  Placement = pos=(50.5,27.5746,125.216) rot=(0.60812,-0.60812,0.510274;2.19793rad)
  SolverId = Asm4EE
  expr: Placement = Fan1Holder.Placement * Mount2.Placement * AttachmentOffset * Fan.Placement ^ -1
FEATURE [App::Link] BottomCover001  label="BottomCover002"
  AttachedBy = #Base001
  AttachedTo = Base002#Bottom
  LinkPlacement = pos=(50.5,29.0518,125.476) rot=(0.60812,-0.60812,0.510274;2.19793rad)
  LinkedObject = -> Body004
  Placement = pos=(50.5,29.0518,125.476) rot=(0.60812,-0.60812,0.510274;2.19793rad)
  SolverId = Asm4EE
  expr: Placement = Base002.Placement * Bottom.Placement * AttachmentOffset * Base001.Placement ^ -1
FEATURE [App::Part] Assembly
  AssemblyType = Part::Link
  Group = -> [LCS_Origin,Constraints,Variables,Configurations,Base,Fan1Holder,Fan2Holder,FilterHolder,FilterHolder001,_0mmAxialFan,_0mmAxialFan001,BottomCover,Base002,BottomCover001]
  Origin = -> Origin001
  Type = Assembly
FEATURE [Sketcher::SketchObject] Sketch031
  ArcFitTolerance = 1e-06
  AttachmentSupport = -> [XZ_Plane]
  FullyConstrained = true
  MakeInternals = false
  MapMode = 5
  Placement = pos=(0,0,0) rot=(1,0,0;1.5708rad)
  sketch-geometry (8):
    g0: LineSegment StartX=0 StartY=0 StartZ=0 EndX=0 EndY=-5 EndZ=0
    g1: LineSegment StartX=0 StartY=-5 StartZ=0 EndX=43 EndY=-5 EndZ=0
    g2: LineSegment StartX=43 StartY=-5 StartZ=0 EndX=43 EndY=1.24e-14 EndZ=0
    g3: LineSegment StartX=43 StartY=1.24e-14 StartZ=0 EndX=0 EndY=0 EndZ=0
    g4: LineSegment StartX=43 StartY=1.24e-14 StartZ=0 EndX=44.7101 EndY=-4.69846 EndZ=0
    g5: LineSegment StartX=44.7101 StartY=-4.69846 StartZ=0 EndX=85.1169 EndY=10.0084 EndZ=0
    g6: LineSegment StartX=85.1169 StartY=10.0084 StartZ=0 EndX=83.4068 EndY=14.7069 EndZ=0
    g7: LineSegment StartX=83.4068 StartY=14.7069 StartZ=0 EndX=43 EndY=1.24e-14 EndZ=0
  constraints (22):
    c: Angle(g-3,g-1) = 1.39626
    c: Coincident(g0,g1)
    c: Coincident(g1,g2)
    c: Coincident(g2,g3)
    c: Coincident(g3,g0)
    c: Vertical(g0)
    c: Vertical(g2)
    c: Horizontal(g1)
    c: Coincident(g0,g-1)
    c: Coincident(g2,g-3)
    c: DistanceY(g2,g2) = 5
    c: Coincident(g2,g4)
    c: Coincident(g4,g5)
    c: Coincident(g5,g6)
    c: Coincident(g6,g7)
    c: Coincident(g7,g4)
    c: Perpendicular(g7,g4)
    c: Perpendicular(g6,g7)
    c: Equal(g4,g6)
    c: Equal(g6,g2)
    c: Equal(g7,g1)
    c: Angle(g7,g-3) = 1.39626
FEATURE [PartDesign::Pocket] Pocket008
  BaseFeature = -> Pad009
  Direction = (0,1,-2e-16)
  Length = 5
  Length2 = 5
  Profile = -> Sketch031
  ReferenceAxis = -> Sketch031 [N_Axis]
  Refine = true
  Reversed = true
  Suppressed = false
  Type = 1
FEATURE [PartDesign::CoordinateSystem] Mount1
  AttacherType = Attacher::AttachEngine3D
  AttachmentSupport = -> [Pocket008]
  MapMode = 45
  Placement = pos=(-50.5,-7e-16,6.5) rot=(0,0.707107,0.707107;3.14159rad)
FEATURE [PartDesign::CoordinateSystem] Mount2
  AttacherType = Attacher::AttachEngine3D
  AttachmentOffset = pos=(0,0,25) rot=(0,0,1;0rad)
  AttachmentSupport = -> [Pocket008]
  MapMode = 11
  Placement = pos=(41.8539,-50.5,6.5) rot=(0.642788,0,0.766044;3.14159rad)
FEATURE [Sketcher::SketchObject] Sketch032
  ArcFitTolerance = 1e-06
  AttachmentSupport = -> [XZ_Plane]
  ExternalGeometry = -> [Pocket008]
  FullyConstrained = true
  MakeInternals = false
  MapMode = 5
  Placement = pos=(0,0,0) rot=(1,0,0;1.5708rad)
  sketch-geometry (7):
    g0: LineSegment StartX=41.2355 StartY=1.5 StartZ=0 EndX=42.7355 EndY=1.5 EndZ=0
    g1: LineSegment StartX=42.7355 StartY=1.5 StartZ=0 EndX=44.145 EndY=2.01303 EndZ=0
    g2: ArcOfCircle CenterX=41.2355 CenterY=2.10733 CenterZ=0 NormalX=0 NormalY=0 NormalZ=1 AngleXU=0 Radius=0.607328 StartAngle=4.71239 EndAngle=6.06406
    g3: ArcOfCircle CenterX=43.9373 CenterY=2.58373 CenterZ=0 NormalX=0 NormalY=0 NormalZ=1 AngleXU=0 Radius=0.607328 StartAngle=3.70978 EndAngle=5.06145
    g4: LineSegment StartX=42.3157 StartY=2.4414 StartZ=0 EndX=42.8081 EndY=2.52822 EndZ=0
    g5: ArcOfCircle CenterX=42.4211 CenterY=1.84329 CenterZ=0 NormalX=0 NormalY=0 NormalZ=1 AngleXU=0 Radius=0.607328 StartAngle=1.74533 EndAngle=2.92247
    g6: ArcOfCircle CenterX=42.9135 CenterY=1.93012 CenterZ=0 NormalX=0 NormalY=0 NormalZ=1 AngleXU=0 Radius=0.607328 StartAngle=0.568188 EndAngle=1.74533
  constraints (17):
    c: Coincident(g0,g-4)
    c: Horizontal(g0)
    c: Coincident(g0,g1)
    c: DistanceX(g0,g0) = 1.5
    c: Angle(g1,g-4) = 1.39626
    c: Symmetric(g4,g4,g-4)
    c: Tangent(g5,g4) = 1.5708
    c: Tangent(g5,g2) = 1.5708
    c: Tangent(g6,g4) = 1.5708
    c: Tangent(g6,g3) = 1.5708
    c: Tangent(g3,g1) = -1.5708
    c: Tangent(g2,g0) = -1.5708
    c: Equal(g2,g5)
    c: Equal(g5,g6)
    c: Equal(g6,g3)
    c: Distance(g0,g4) = 1
    c: Distance(g4) = 0.5
FEATURE [PartDesign::AdditivePipe] AdditivePipe002
  AuxilleryCurvelinear = true
  AuxillerySpineTangent = false
  BaseFeature = -> Pocket008
  Binormal = (0,0,0)
  Mode = 0
  Profile = -> Sketch032
  Refine = true
  Spine = -> Pocket008 [Edge31,Edge30,Edge29,Edge28,Edge32,Edge33,Edge34,Edge35,Edge27]
  SpineTangent = false
  Suppressed = false
  Transformation = 0
  Transition = 1
FEATURE [PartDesign::Body] Body  label="Fan1Holder"
  AllowCompound = false
  Group = -> [Sketch,Pad,Sketch001,Pad001,Sketch002,AdditivePipe,Sketch003,Pad002,LinearPattern,Sketch004,Pad003,LinearPattern001,FanMountHole,Sketch005,Pocket,OtherFanHolder,FilterHolderMount,Sketch010,Pad008,Sketch011,Pad009,Mount1,Mount2,Sketch031,Pocket008,Sketch032,AdditivePipe002]
  Origin = -> Origin
  Tip = -> AdditivePipe002
FEATURE [Sketcher::SketchObject] Sketch033
  ArcFitTolerance = 1e-06
  AttachmentSupport = -> [Pad007]
  ExternalGeometry = -> [Pad007]
  FullyConstrained = true
  MakeInternals = false
  MapMode = 5
  Placement = pos=(0,0,1.5) rot=(0,0,1;0rad)
  sketch-geometry (8):
    g0: Circle CenterX=35.75 CenterY=35.75 CenterZ=0 NormalX=0 NormalY=0 NormalZ=1 AngleXU=0 Radius=2.5
    g1: Circle CenterX=35.75 CenterY=35.75 CenterZ=0 NormalX=0 NormalY=0 NormalZ=1 AngleXU=0 Radius=3.64645
    g2: Circle CenterX=-35.75 CenterY=35.75 CenterZ=0 NormalX=0 NormalY=0 NormalZ=1 AngleXU=0 Radius=2.5
    g3: Circle CenterX=-35.75 CenterY=35.75 CenterZ=0 NormalX=0 NormalY=0 NormalZ=1 AngleXU=0 Radius=3.64645
    g4: Circle CenterX=-35.75 CenterY=-35.75 CenterZ=0 NormalX=0 NormalY=0 NormalZ=1 AngleXU=0 Radius=2.5
    g5: Circle CenterX=-35.75 CenterY=-35.75 CenterZ=0 NormalX=0 NormalY=0 NormalZ=1 AngleXU=0 Radius=3.64645
    g6: Circle CenterX=35.75 CenterY=-35.75 CenterZ=0 NormalX=0 NormalY=0 NormalZ=1 AngleXU=0 Radius=2.5
    g7: Circle CenterX=35.75 CenterY=-35.75 CenterZ=0 NormalX=0 NormalY=0 NormalZ=1 AngleXU=0 Radius=3.64645
  constraints (16):
    c: Coincident(g0,g-3)
    c: Coincident(g1,g0)
    c: Coincident(g2,g-6)
    c: Coincident(g3,g2)
    c: Coincident(g4,g-5)
    c: Coincident(g5,g4)
    c: Coincident(g6,g-4)
    c: Coincident(g7,g6)
    c: Equal(g6,g4)
    c: Equal(g4,g2)
    c: Equal(g2,g0)
    c: Equal(g0,g-4)
    c: Equal(g7,g1)
    c: Equal(g1,g3)
    c: Equal(g3,g5)
    c: Tangent(g7,g-7)
FEATURE [PartDesign::Pad] Pad017
  BaseFeature = -> Pad007
  Direction = (0,0,1)
  Length = 10
  Length2 = 10
  Profile = -> Sketch033
  ReferenceAxis = -> Sketch033 [N_Axis]
  Refine = true
  Suppressed = false
  Type = 3
  UpToFace = -> Pad007 [Face132]
FEATURE [PartDesign::Body] Body001  label="FilterHolder"
  AllowCompound = false
  Group = -> [Sketch006,Pad004,Sketch007,Pad005,LinearPattern002,Sketch008,Pad006,LinearPattern003,Sketch009,Pad007,FanHolder,Sketch033,Pad017]
  Origin = -> Origin002
  Tip = -> Pad017
FEATURE [App::DocumentObjectGroup] Parts
  Group = -> [Body,Body001,Body002,Body003,Body004]
